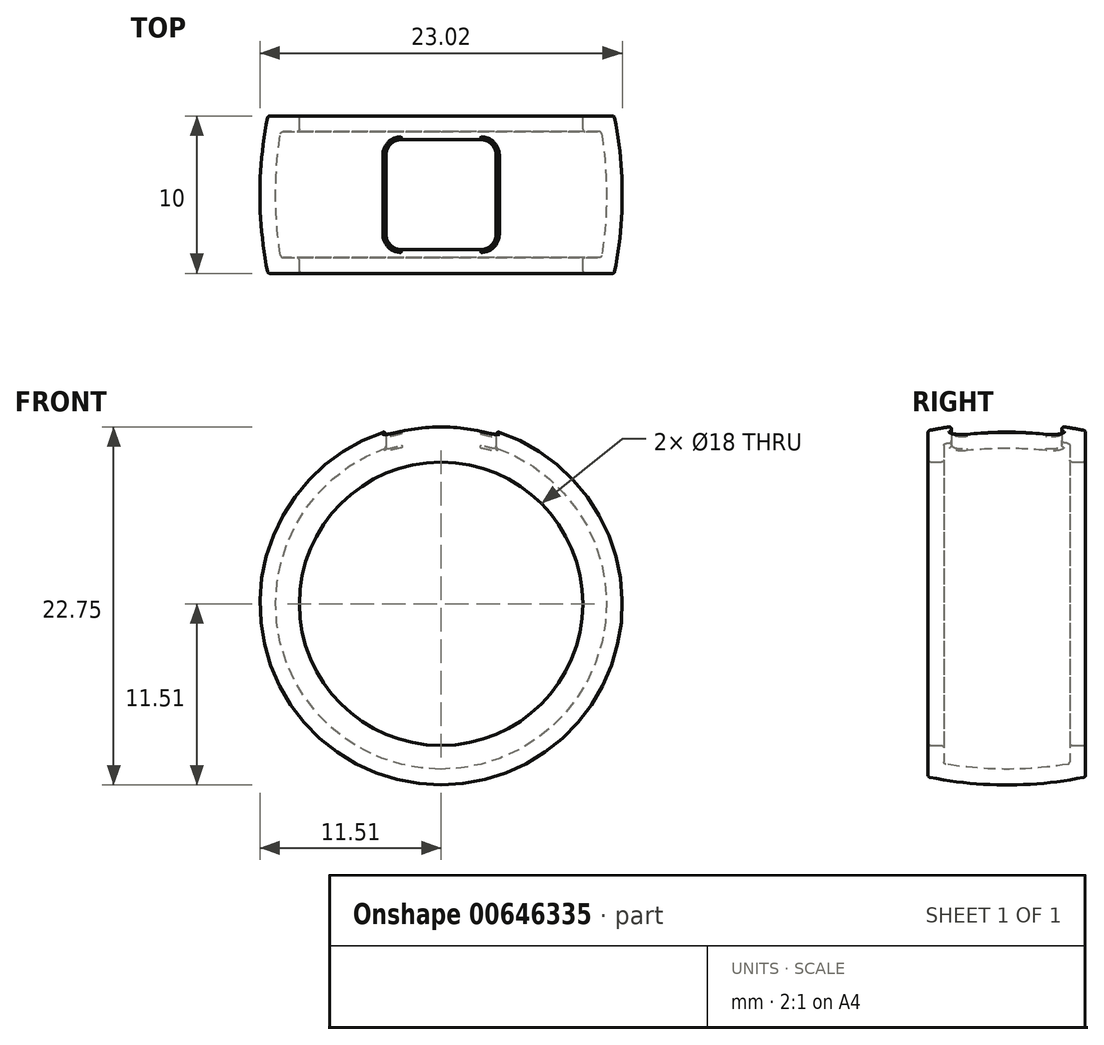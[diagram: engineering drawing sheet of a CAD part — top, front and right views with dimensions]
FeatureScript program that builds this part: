
annotation { "Feature Type Name" : "Feature", "Feature Type Description" : "" }
export const myFeature = defineFeature(function(context is Context, id is Id, definition is map)
    precondition{}
    {
        {
            var Q0;
            Q0=qCreatedBy(makeId("Top.planeOp"),FACE);
            var sketch = newSketch(context, id + "F0", { "sketchPlane" : qUnion([Q0])});
            skLineSegment(sketch, "E0", {"start": v(0, 0) * mm, "end": v(-9, 0) * mm, "construction": true});
            skLineSegment(sketch, "E1", {"start": v(-9, 5) * mm, "end": v(-9, -5) * mm});
            skLineSegment(sketch, "E2", {"start": v(-9, -5) * mm, "end": v(-11, -5) * mm});
            skLineSegment(sketch, "E3", {"start": v(-9, 5) * mm, "end": v(-11, 5) * mm});
            skArc(sketch, "E4", {"start": v(-11, 5) * mm, "mid": v(-11.5, 0) * mm, "end": v(-11, -5) * mm});
            skLineSegment(sketch, "E5", {"start": v(0, 0) * mm, "end": v(0, -20.5) * mm, "construction": true});
            skSolve(sketch);
        }
        {
            var Q0;
            Q0=makeQuery(id+"F0.imprint","IMPRINT",FACE,{"disambiguationData":[TD([[makeQuery(id+"F0.imprint","IMPRINT",EDGE,{"derivedFrom":sQuery(id+"F0.wireOp",EDGE,"E1")}),-1.0]])]});
            var Q1;
            Q1=sQuery(id+"F0.wireOp",EDGE,"E5");
            revolve(context, id + "F1", {"entities" : qUnion([Q0]), "axis" : qUnion([Q1]), "revolveType" : RevolveType.FULL});
        }
        {
            var Q0;
            Q0=makeQuery(id+"F1.opRevolve","SWEPT_FACE",FACE,{"disambiguationData":[OSD([sQuery(id+"F0.wireOp",EDGE,"E1")])]});
            shell(context, id + "F2", {"entities" : qUnion([Q0]), "thickness" : 1 * mm});
        }
        {
            var Q0;
            Q0=qCreatedBy(makeId("Top.planeOp"),FACE);
            var sketch = newSketch(context, id + "F3", { "sketchPlane" : qUnion([Q0])});
            skLineSegment(sketch, "E6.bottom", {"start": v(2.5, -3.5) * mm, "end": v(-2.5, -3.5) * mm});
            skLineSegment(sketch, "E6.top", {"start": v(2.5, 3.5) * mm, "end": v(-2.5, 3.5) * mm});
            skLineSegment(sketch, "E6.left", {"start": v(3.5, -2.5) * mm, "end": v(3.5, 2.5) * mm});
            skLineSegment(sketch, "E6.right", {"start": v(-3.5, -2.5) * mm, "end": v(-3.5, 2.5) * mm});
            skPoint(sketch, "E6.middle", {"position": v(0, 0) * mm});
            skPoint(sketch, "E7.visualSharp", {"position": v(-3.5, 3.5) * mm});
            skArc(sketch, "E7.filletArc", {"start": v(-2.5, 3.5) * mm, "mid": v(-3.2, 3.2) * mm, "end": v(-3.5, 2.5) * mm});
            skPoint(sketch, "E8.visualSharp", {"position": v(3.5, 3.5) * mm});
            skArc(sketch, "E8.filletArc", {"start": v(3.5, 2.5) * mm, "mid": v(3.2, 3.2) * mm, "end": v(2.5, 3.5) * mm});
            skPoint(sketch, "E9.visualSharp", {"position": v(-3.5, -3.5) * mm});
            skArc(sketch, "E9.filletArc", {"start": v(-3.5, -2.5) * mm, "mid": v(-3.2, -3.2) * mm, "end": v(-2.5, -3.5) * mm});
            skPoint(sketch, "E10.visualSharp", {"position": v(3.5, -3.5) * mm});
            skArc(sketch, "E10.filletArc", {"start": v(2.5, -3.5) * mm, "mid": v(3.2, -3.2) * mm, "end": v(3.5, -2.5) * mm});
            skSolve(sketch);
        }
        {
            var Q0;
            Q0 = qSketchRegion(id + "F3", true);
            extrude(context, id + "F4", {"entities" : qUnion([Q0]), "operationType" : NewBodyOperationType.REMOVE, "endBound" : BoundingType.THROUGH_ALL, "depth" : 25 * mm, "offsetDistance" : 25 * mm});
        }
        {
            var Q0;
            Q0=makeQuery(id+"F1.opRevolve","SWEPT_EDGE",EDGE,{"disambiguationData":[OSD([sQuery(id+"F0.wireOp",EDGE,"E1"),sQuery(id+"F0.wireOp",EDGE,"E3")])]});
            var Q1;
            Q1=makeQuery(id+"F1.opRevolve","SWEPT_EDGE",EDGE,{"disambiguationData":[OSD([sQuery(id+"F0.wireOp",EDGE,"E3"),sQuery(id+"F0.wireOp",EDGE,"E4")])]});
            var Q2;
            Q2=makeQuery(id+"FRUT5MbfFa7QnNZ_1.6.F4.boolean.opBoolean","INTERSECT",EDGE,{"derivedFrom":[makeQuery(id+"F2.opShell","OFFSET_FACE",FACE,{"disambiguationData":[OSD([sQuery(id+"F0.wireOp",EDGE,"E4")])]}),makeQuery(id+"FRUT5MbfFa7QnNZ_1.6.F4.opExtrude","SWEPT_FACE",FACE,{"disambiguationData":[OSD([sQuery(id+"F3.wireOp",EDGE,"E6.top")])]})]});
            var Q3;
            Q3=makeQuery(id+"FRUT5MbfFa7QnNZ_1.5.F4.boolean.opBoolean","INTERSECT",EDGE,{"derivedFrom":[makeQuery(id+"F2.opShell","OFFSET_FACE",FACE,{"disambiguationData":[OSD([sQuery(id+"F0.wireOp",EDGE,"E4")])]}),makeQuery(id+"FRUT5MbfFa7QnNZ_1.5.F4.opExtrude","SWEPT_FACE",FACE,{"disambiguationData":[OSD([sQuery(id+"F3.wireOp",EDGE,"E6.left")])]})]});
            var Q4;
            Q4=makeQuery(id+"FRUT5MbfFa7QnNZ_1.3.F4.boolean.opBoolean","INTERSECT",EDGE,{"derivedFrom":[makeQuery(id+"F2.opShell","OFFSET_FACE",FACE,{"disambiguationData":[OSD([sQuery(id+"F0.wireOp",EDGE,"E4")])]}),makeQuery(id+"FRUT5MbfFa7QnNZ_1.3.F4.opExtrude","SWEPT_FACE",FACE,{"disambiguationData":[OSD([sQuery(id+"F3.wireOp",EDGE,"E6.top")])]})]});
            var Q5;
            Q5=makeQuery(id+"FRUT5MbfFa7QnNZ_1.5.F4.boolean.opBoolean","INTERSECT",EDGE,{"derivedFrom":[makeQuery(id+"F2.opShell","OFFSET_FACE",FACE,{"disambiguationData":[OSD([sQuery(id+"F0.wireOp",EDGE,"E4")])]}),makeQuery(id+"FRUT5MbfFa7QnNZ_1.5.F4.opExtrude","SWEPT_FACE",FACE,{"disambiguationData":[OSD([sQuery(id+"F3.wireOp",EDGE,"E6.top")])]})]});
            var Q6;
            Q6=makeQuery(id+"FRUT5MbfFa7QnNZ_1.2.F4.boolean.opBoolean","INTERSECT",EDGE,{"derivedFrom":[makeQuery(id+"F2.opShell","OFFSET_FACE",FACE,{"disambiguationData":[OSD([sQuery(id+"F0.wireOp",EDGE,"E4")])]}),makeQuery(id+"FRUT5MbfFa7QnNZ_1.2.F4.opExtrude","SWEPT_FACE",FACE,{"disambiguationData":[OSD([sQuery(id+"F3.wireOp",EDGE,"E6.top")])]})]});
            var Q7;
            Q7=makeQuery(id+"FRUT5MbfFa7QnNZ_1.6.F4.boolean.opBoolean","INTERSECT",EDGE,{"derivedFrom":[makeQuery(id+"F2.opShell","OFFSET_FACE",FACE,{"disambiguationData":[OSD([sQuery(id+"F0.wireOp",EDGE,"E4")])]}),makeQuery(id+"FRUT5MbfFa7QnNZ_1.6.F4.opExtrude","SWEPT_FACE",FACE,{"disambiguationData":[OSD([sQuery(id+"F3.wireOp",EDGE,"E6.right")])]})]});
            var Q8;
            Q8=makeQuery(id+"FRUT5MbfFa7QnNZ_1.2.F4.boolean.opBoolean","INTERSECT",EDGE,{"derivedFrom":[makeQuery(id+"F2.opShell","OFFSET_FACE",FACE,{"disambiguationData":[OSD([sQuery(id+"F0.wireOp",EDGE,"E4")])]}),makeQuery(id+"FRUT5MbfFa7QnNZ_1.2.F4.opExtrude","SWEPT_FACE",FACE,{"disambiguationData":[OSD([sQuery(id+"F3.wireOp",EDGE,"E6.left")])]})]});
            var Q9;
            Q9=makeQuery(id+"F2.opShell","OFFSET_EDGE",EDGE,{"disambiguationData":[OSD([sQuery(id+"F0.wireOp",EDGE,"E3"),sQuery(id+"F0.wireOp",EDGE,"E4")])]});
            var Q10;
            Q10=makeQuery(id+"FRUT5MbfFa7QnNZ_1.4.F4.boolean.opBoolean","INTERSECT",EDGE,{"derivedFrom":[makeQuery(id+"F1.opRevolve","SWEPT_FACE",FACE,{"disambiguationData":[OSD([sQuery(id+"F0.wireOp",EDGE,"E4")])]}),makeQuery(id+"FRUT5MbfFa7QnNZ_1.4.F4.opExtrude","SWEPT_FACE",FACE,{"disambiguationData":[OSD([sQuery(id+"F3.wireOp",EDGE,"E6.bottom")])]})]});
            var Q11;
            Q11=makeQuery(id+"FRUT5MbfFa7QnNZ_1.4.F4.boolean.opBoolean","INTERSECT",EDGE,{"derivedFrom":[makeQuery(id+"F1.opRevolve","SWEPT_FACE",FACE,{"disambiguationData":[OSD([sQuery(id+"F0.wireOp",EDGE,"E4")])]}),makeQuery(id+"FRUT5MbfFa7QnNZ_1.4.F4.opExtrude","SWEPT_FACE",FACE,{"disambiguationData":[OSD([sQuery(id+"F3.wireOp",EDGE,"E6.left")])]})]});
            var Q12;
            Q12=makeQuery(id+"FRUT5MbfFa7QnNZ_1.5.F4.boolean.opBoolean","INTERSECT",EDGE,{"derivedFrom":[makeQuery(id+"F1.opRevolve","SWEPT_FACE",FACE,{"disambiguationData":[OSD([sQuery(id+"F0.wireOp",EDGE,"E4")])]}),makeQuery(id+"FRUT5MbfFa7QnNZ_1.5.F4.opExtrude","SWEPT_FACE",FACE,{"disambiguationData":[OSD([sQuery(id+"F3.wireOp",EDGE,"E6.right")])]})]});
            var Q13;
            Q13=makeQuery(id+"F1.opRevolve","SWEPT_EDGE",EDGE,{"disambiguationData":[OSD([sQuery(id+"F0.wireOp",EDGE,"E1"),sQuery(id+"F0.wireOp",EDGE,"E2")])]});
            var Q14;
            Q14=makeQuery(id+"F2.opShell","OFFSET_EDGE",EDGE,{"disambiguationData":[OSD([sQuery(id+"F0.wireOp",EDGE,"E1"),sQuery(id+"F0.wireOp",EDGE,"E3")])]});
            var Q15;
            Q15=makeQuery(id+"FRUT5MbfFa7QnNZ_1.4.F4.boolean.opBoolean","INTERSECT",EDGE,{"derivedFrom":[makeQuery(id+"F1.opRevolve","SWEPT_FACE",FACE,{"disambiguationData":[OSD([sQuery(id+"F0.wireOp",EDGE,"E4")])]}),makeQuery(id+"FRUT5MbfFa7QnNZ_1.4.F4.opExtrude","SWEPT_FACE",FACE,{"disambiguationData":[OSD([sQuery(id+"F3.wireOp",EDGE,"E6.top")])]})]});
            var Q16;
            Q16=makeQuery(id+"FRUT5MbfFa7QnNZ_1.5.F4.boolean.opBoolean","INTERSECT",EDGE,{"derivedFrom":[makeQuery(id+"F1.opRevolve","SWEPT_FACE",FACE,{"disambiguationData":[OSD([sQuery(id+"F0.wireOp",EDGE,"E4")])]}),makeQuery(id+"FRUT5MbfFa7QnNZ_1.5.F4.opExtrude","SWEPT_FACE",FACE,{"disambiguationData":[OSD([sQuery(id+"F3.wireOp",EDGE,"E6.bottom")])]})]});
            var Q17;
            Q17=makeQuery(id+"FRUT5MbfFa7QnNZ_1.5.F4.boolean.opBoolean","INTERSECT",EDGE,{"derivedFrom":[makeQuery(id+"F1.opRevolve","SWEPT_FACE",FACE,{"disambiguationData":[OSD([sQuery(id+"F0.wireOp",EDGE,"E4")])]}),makeQuery(id+"FRUT5MbfFa7QnNZ_1.5.F4.opExtrude","SWEPT_FACE",FACE,{"disambiguationData":[OSD([sQuery(id+"F3.wireOp",EDGE,"E6.left")])]})]});
            var Q18;
            Q18=makeQuery(id+"FRUT5MbfFa7QnNZ_1.6.F4.boolean.opBoolean","INTERSECT",EDGE,{"derivedFrom":[makeQuery(id+"F1.opRevolve","SWEPT_FACE",FACE,{"disambiguationData":[OSD([sQuery(id+"F0.wireOp",EDGE,"E4")])]}),makeQuery(id+"FRUT5MbfFa7QnNZ_1.6.F4.opExtrude","SWEPT_FACE",FACE,{"disambiguationData":[OSD([sQuery(id+"F3.wireOp",EDGE,"E6.right")])]})]});
            var Q19;
            Q19=makeQuery(id+"FRUT5MbfFa7QnNZ_1.6.F4.boolean.opBoolean","INTERSECT",EDGE,{"derivedFrom":[makeQuery(id+"F1.opRevolve","SWEPT_FACE",FACE,{"disambiguationData":[OSD([sQuery(id+"F0.wireOp",EDGE,"E4")])]}),makeQuery(id+"FRUT5MbfFa7QnNZ_1.6.F4.opExtrude","SWEPT_FACE",FACE,{"disambiguationData":[OSD([sQuery(id+"F3.wireOp",EDGE,"E6.bottom")])]})]});
            var Q20;
            Q20=makeQuery(id+"FRUT5MbfFa7QnNZ_1.6.F4.boolean.opBoolean","INTERSECT",EDGE,{"derivedFrom":[makeQuery(id+"F1.opRevolve","SWEPT_FACE",FACE,{"disambiguationData":[OSD([sQuery(id+"F0.wireOp",EDGE,"E4")])]}),makeQuery(id+"FRUT5MbfFa7QnNZ_1.6.F4.opExtrude","SWEPT_FACE",FACE,{"disambiguationData":[OSD([sQuery(id+"F3.wireOp",EDGE,"E6.left")])]})]});
            var Q21;
            Q21=makeQuery(id+"FRUT5MbfFa7QnNZ_1.6.F4.boolean.opBoolean","INTERSECT",EDGE,{"derivedFrom":[makeQuery(id+"F1.opRevolve","SWEPT_FACE",FACE,{"disambiguationData":[OSD([sQuery(id+"F0.wireOp",EDGE,"E4")])]}),makeQuery(id+"FRUT5MbfFa7QnNZ_1.6.F4.opExtrude","SWEPT_FACE",FACE,{"disambiguationData":[OSD([sQuery(id+"F3.wireOp",EDGE,"E6.top")])]})]});
            var Q22;
            Q22=makeQuery(id+"FRUT5MbfFa7QnNZ_1.1.F4.boolean.opBoolean","INTERSECT",EDGE,{"derivedFrom":[makeQuery(id+"F2.opShell","OFFSET_FACE",FACE,{"disambiguationData":[OSD([sQuery(id+"F0.wireOp",EDGE,"E4")])]}),makeQuery(id+"FRUT5MbfFa7QnNZ_1.1.F4.opExtrude","SWEPT_FACE",FACE,{"disambiguationData":[OSD([sQuery(id+"F3.wireOp",EDGE,"E6.right")])]})]});
            var Q23;
            Q23=makeQuery(id+"FRUT5MbfFa7QnNZ_1.5.F4.boolean.opBoolean","INTERSECT",EDGE,{"derivedFrom":[makeQuery(id+"F1.opRevolve","SWEPT_FACE",FACE,{"disambiguationData":[OSD([sQuery(id+"F0.wireOp",EDGE,"E4")])]}),makeQuery(id+"FRUT5MbfFa7QnNZ_1.5.F4.opExtrude","SWEPT_FACE",FACE,{"disambiguationData":[OSD([sQuery(id+"F3.wireOp",EDGE,"E6.top")])]})]});
            var Q24;
            Q24=makeQuery(id+"FRUT5MbfFa7QnNZ_1.1.F4.boolean.opBoolean","INTERSECT",EDGE,{"derivedFrom":[makeQuery(id+"F2.opShell","OFFSET_FACE",FACE,{"disambiguationData":[OSD([sQuery(id+"F0.wireOp",EDGE,"E4")])]}),makeQuery(id+"FRUT5MbfFa7QnNZ_1.1.F4.opExtrude","SWEPT_FACE",FACE,{"disambiguationData":[OSD([sQuery(id+"F3.wireOp",EDGE,"E6.top")])]})]});
            var Q25;
            Q25=makeQuery(id+"F2.opShell","OFFSET_EDGE",EDGE,{"disambiguationData":[OSD([sQuery(id+"F0.wireOp",EDGE,"E1"),sQuery(id+"F0.wireOp",EDGE,"E2")])]});
            var Q26;
            Q26=makeQuery(id+"F4.boolean.opBoolean","INTERSECT",EDGE,{"derivedFrom":[makeQuery(id+"F2.opShell","OFFSET_FACE",FACE,{"disambiguationData":[OSD([sQuery(id+"F0.wireOp",EDGE,"E4")])]}),makeQuery(id+"F4.opExtrude","SWEPT_FACE",FACE,{"disambiguationData":[OSD([sQuery(id+"F3.wireOp",EDGE,"E6.right")])]})]});
            var Q27;
            Q27=makeQuery(id+"F4.boolean.opBoolean","INTERSECT",EDGE,{"derivedFrom":[makeQuery(id+"F2.opShell","OFFSET_FACE",FACE,{"disambiguationData":[OSD([sQuery(id+"F0.wireOp",EDGE,"E4")])]}),makeQuery(id+"F4.opExtrude","SWEPT_FACE",FACE,{"disambiguationData":[OSD([sQuery(id+"F3.wireOp",EDGE,"E6.top")])]})]});
            var Q28;
            Q28=makeQuery(id+"FRUT5MbfFa7QnNZ_1.3.F4.boolean.opBoolean","INTERSECT",EDGE,{"derivedFrom":[makeQuery(id+"F2.opShell","OFFSET_FACE",FACE,{"disambiguationData":[OSD([sQuery(id+"F0.wireOp",EDGE,"E4")])]}),makeQuery(id+"FRUT5MbfFa7QnNZ_1.3.F4.opExtrude","SWEPT_FACE",FACE,{"disambiguationData":[OSD([sQuery(id+"F3.wireOp",EDGE,"E6.left")])]})]});
            var Q29;
            Q29=makeQuery(id+"FRUT5MbfFa7QnNZ_1.4.F4.boolean.opBoolean","COPY",EDGE,{"derivedFrom":makeQuery(id+"FRUT5MbfFa7QnNZ_1.4.F4.opExtrude","SWEPT_EDGE",EDGE,{"disambiguationData":[OSD([sQuery(id+"F3.wireOp",EDGE,"E6.top"),sQuery(id+"F3.wireOp",EDGE,"E8.filletArc")])]})});
            var Q30;
            Q30=makeQuery(id+"FRUT5MbfFa7QnNZ_1.2.F4.boolean.opBoolean","INTERSECT",EDGE,{"derivedFrom":[makeQuery(id+"F2.opShell","OFFSET_FACE",FACE,{"disambiguationData":[OSD([sQuery(id+"F0.wireOp",EDGE,"E4")])]}),makeQuery(id+"FRUT5MbfFa7QnNZ_1.2.F4.opExtrude","SWEPT_FACE",FACE,{"disambiguationData":[OSD([sQuery(id+"F3.wireOp",EDGE,"E6.right")])]})]});
            var Q31;
            Q31=makeQuery(id+"F1.opRevolve","SWEPT_EDGE",EDGE,{"disambiguationData":[OSD([sQuery(id+"F0.wireOp",EDGE,"E2"),sQuery(id+"F0.wireOp",EDGE,"E4")])]});
            var Q32;
            Q32=makeQuery(id+"F4.boolean.opBoolean","INTERSECT",EDGE,{"derivedFrom":[makeQuery(id+"F1.opRevolve","SWEPT_FACE",FACE,{"disambiguationData":[OSD([sQuery(id+"F0.wireOp",EDGE,"E4")])]}),makeQuery(id+"F4.opExtrude","SWEPT_FACE",FACE,{"disambiguationData":[OSD([sQuery(id+"F3.wireOp",EDGE,"E6.right")])]})]});
            var Q33;
            Q33=makeQuery(id+"F4.boolean.opBoolean","INTERSECT",EDGE,{"derivedFrom":[makeQuery(id+"F1.opRevolve","SWEPT_FACE",FACE,{"disambiguationData":[OSD([sQuery(id+"F0.wireOp",EDGE,"E4")])]}),makeQuery(id+"F4.opExtrude","SWEPT_FACE",FACE,{"disambiguationData":[OSD([sQuery(id+"F3.wireOp",EDGE,"E6.bottom")])]})]});
            var Q34;
            Q34=makeQuery(id+"F4.boolean.opBoolean","INTERSECT",EDGE,{"derivedFrom":[makeQuery(id+"F1.opRevolve","SWEPT_FACE",FACE,{"disambiguationData":[OSD([sQuery(id+"F0.wireOp",EDGE,"E4")])]}),makeQuery(id+"F4.opExtrude","SWEPT_FACE",FACE,{"disambiguationData":[OSD([sQuery(id+"F3.wireOp",EDGE,"E6.top")])]})]});
            var Q35;
            Q35=makeQuery(id+"F4.boolean.opBoolean","INTERSECT",EDGE,{"derivedFrom":[makeQuery(id+"F1.opRevolve","SWEPT_FACE",FACE,{"disambiguationData":[OSD([sQuery(id+"F0.wireOp",EDGE,"E4")])]}),makeQuery(id+"F4.opExtrude","SWEPT_FACE",FACE,{"disambiguationData":[OSD([sQuery(id+"F3.wireOp",EDGE,"E6.left")])]})]});
            var Q36;
            Q36=makeQuery(id+"FRUT5MbfFa7QnNZ_1.1.F4.boolean.opBoolean","INTERSECT",EDGE,{"derivedFrom":[makeQuery(id+"F1.opRevolve","SWEPT_FACE",FACE,{"disambiguationData":[OSD([sQuery(id+"F0.wireOp",EDGE,"E4")])]}),makeQuery(id+"FRUT5MbfFa7QnNZ_1.1.F4.opExtrude","SWEPT_FACE",FACE,{"disambiguationData":[OSD([sQuery(id+"F3.wireOp",EDGE,"E6.right")])]})]});
            var Q37;
            Q37=makeQuery(id+"FRUT5MbfFa7QnNZ_1.2.F4.boolean.opBoolean","INTERSECT",EDGE,{"derivedFrom":[makeQuery(id+"F1.opRevolve","SWEPT_FACE",FACE,{"disambiguationData":[OSD([sQuery(id+"F0.wireOp",EDGE,"E4")])]}),makeQuery(id+"FRUT5MbfFa7QnNZ_1.2.F4.opExtrude","SWEPT_FACE",FACE,{"disambiguationData":[OSD([sQuery(id+"F3.wireOp",EDGE,"E6.top")])]})]});
            var Q38;
            Q38=makeQuery(id+"FRUT5MbfFa7QnNZ_1.3.F4.boolean.opBoolean","INTERSECT",EDGE,{"derivedFrom":[makeQuery(id+"F1.opRevolve","SWEPT_FACE",FACE,{"disambiguationData":[OSD([sQuery(id+"F0.wireOp",EDGE,"E4")])]}),makeQuery(id+"FRUT5MbfFa7QnNZ_1.3.F4.opExtrude","SWEPT_FACE",FACE,{"disambiguationData":[OSD([sQuery(id+"F3.wireOp",EDGE,"E6.top")])]})]});
            var Q39;
            Q39=makeQuery(id+"FRUT5MbfFa7QnNZ_1.3.F4.boolean.opBoolean","INTERSECT",EDGE,{"derivedFrom":[makeQuery(id+"F1.opRevolve","SWEPT_FACE",FACE,{"disambiguationData":[OSD([sQuery(id+"F0.wireOp",EDGE,"E4")])]}),makeQuery(id+"FRUT5MbfFa7QnNZ_1.3.F4.opExtrude","SWEPT_FACE",FACE,{"disambiguationData":[OSD([sQuery(id+"F3.wireOp",EDGE,"E6.left")])]})]});
            var Q40;
            Q40=makeQuery(id+"FRUT5MbfFa7QnNZ_1.4.F4.boolean.opBoolean","INTERSECT",EDGE,{"derivedFrom":[makeQuery(id+"F1.opRevolve","SWEPT_FACE",FACE,{"disambiguationData":[OSD([sQuery(id+"F0.wireOp",EDGE,"E4")])]}),makeQuery(id+"FRUT5MbfFa7QnNZ_1.4.F4.opExtrude","SWEPT_FACE",FACE,{"disambiguationData":[OSD([sQuery(id+"F3.wireOp",EDGE,"E6.right")])]})]});
            var Q41;
            Q41=makeQuery(id+"FRUT5MbfFa7QnNZ_1.2.F4.boolean.opBoolean","INTERSECT",EDGE,{"derivedFrom":[makeQuery(id+"F1.opRevolve","SWEPT_FACE",FACE,{"disambiguationData":[OSD([sQuery(id+"F0.wireOp",EDGE,"E4")])]}),makeQuery(id+"FRUT5MbfFa7QnNZ_1.2.F4.opExtrude","SWEPT_FACE",FACE,{"disambiguationData":[OSD([sQuery(id+"F3.wireOp",EDGE,"E6.right")])]})]});
            var Q42;
            Q42=makeQuery(id+"FRUT5MbfFa7QnNZ_1.5.F4.boolean.opBoolean","COPY",EDGE,{"derivedFrom":makeQuery(id+"FRUT5MbfFa7QnNZ_1.5.F4.opExtrude","SWEPT_EDGE",EDGE,{"disambiguationData":[OSD([sQuery(id+"F3.wireOp",EDGE,"E6.left"),sQuery(id+"F3.wireOp",EDGE,"E10.filletArc")])]})});
            var Q43;
            Q43=makeQuery(id+"FRUT5MbfFa7QnNZ_1.3.F4.boolean.opBoolean","COPY",EDGE,{"derivedFrom":makeQuery(id+"FRUT5MbfFa7QnNZ_1.3.F4.opExtrude","SWEPT_EDGE",EDGE,{"disambiguationData":[OSD([sQuery(id+"F3.wireOp",EDGE,"E6.left"),sQuery(id+"F3.wireOp",EDGE,"E8.filletArc")])]})});
            var Q44;
            Q44=makeQuery(id+"FRUT5MbfFa7QnNZ_1.5.F4.boolean.opBoolean","INTERSECT",EDGE,{"derivedFrom":[makeQuery(id+"F2.opShell","OFFSET_FACE",FACE,{"disambiguationData":[OSD([sQuery(id+"F0.wireOp",EDGE,"E4")])]}),makeQuery(id+"FRUT5MbfFa7QnNZ_1.5.F4.opExtrude","SWEPT_FACE",FACE,{"disambiguationData":[OSD([sQuery(id+"F3.wireOp",EDGE,"E10.filletArc")])]})]});
            var Q45;
            Q45=makeQuery(id+"F4.boolean.opBoolean","COPY",EDGE,{"derivedFrom":makeQuery(id+"F4.opExtrude","SWEPT_EDGE",EDGE,{"disambiguationData":[OSD([sQuery(id+"F3.wireOp",EDGE,"E6.left"),sQuery(id+"F3.wireOp",EDGE,"E10.filletArc")])]})});
            var Q46;
            Q46=makeQuery(id+"FRUT5MbfFa7QnNZ_1.6.F4.boolean.opBoolean","COPY",EDGE,{"derivedFrom":makeQuery(id+"FRUT5MbfFa7QnNZ_1.6.F4.opExtrude","SWEPT_EDGE",EDGE,{"disambiguationData":[OSD([sQuery(id+"F3.wireOp",EDGE,"E6.left"),sQuery(id+"F3.wireOp",EDGE,"E8.filletArc")])]})});
            var Q47;
            Q47=makeQuery(id+"FRUT5MbfFa7QnNZ_1.6.F4.boolean.opBoolean","COPY",EDGE,{"derivedFrom":makeQuery(id+"FRUT5MbfFa7QnNZ_1.6.F4.opExtrude","SWEPT_EDGE",EDGE,{"disambiguationData":[OSD([sQuery(id+"F3.wireOp",EDGE,"E6.right"),sQuery(id+"F3.wireOp",EDGE,"E9.filletArc")])]})});
            var Q48;
            Q48=makeQuery(id+"F4.boolean.opBoolean","COPY",EDGE,{"derivedFrom":makeQuery(id+"F4.opExtrude","SWEPT_EDGE",EDGE,{"disambiguationData":[OSD([sQuery(id+"F3.wireOp",EDGE,"E6.top"),sQuery(id+"F3.wireOp",EDGE,"E7.filletArc")])]})});
            var Q49;
            Q49=makeQuery(id+"FRUT5MbfFa7QnNZ_1.3.F4.boolean.opBoolean","COPY",EDGE,{"derivedFrom":makeQuery(id+"FRUT5MbfFa7QnNZ_1.3.F4.opExtrude","SWEPT_EDGE",EDGE,{"disambiguationData":[OSD([sQuery(id+"F3.wireOp",EDGE,"E6.left"),sQuery(id+"F3.wireOp",EDGE,"E10.filletArc")])]})});
            var Q50;
            Q50=makeQuery(id+"FRUT5MbfFa7QnNZ_1.5.F4.boolean.opBoolean","COPY",EDGE,{"derivedFrom":makeQuery(id+"FRUT5MbfFa7QnNZ_1.5.F4.opExtrude","SWEPT_EDGE",EDGE,{"disambiguationData":[OSD([sQuery(id+"F3.wireOp",EDGE,"E6.right"),sQuery(id+"F3.wireOp",EDGE,"E7.filletArc")])]})});
            var Q51;
            Q51=makeQuery(id+"FRUT5MbfFa7QnNZ_1.4.F4.boolean.opBoolean","COPY",EDGE,{"derivedFrom":makeQuery(id+"FRUT5MbfFa7QnNZ_1.4.F4.opExtrude","SWEPT_EDGE",EDGE,{"disambiguationData":[OSD([sQuery(id+"F3.wireOp",EDGE,"E6.left"),sQuery(id+"F3.wireOp",EDGE,"E8.filletArc")])]})});
            var Q52;
            Q52=makeQuery(id+"FRUT5MbfFa7QnNZ_1.1.F4.boolean.opBoolean","INTERSECT",EDGE,{"derivedFrom":[makeQuery(id+"F2.opShell","OFFSET_FACE",FACE,{"disambiguationData":[OSD([sQuery(id+"F0.wireOp",EDGE,"E4")])]}),makeQuery(id+"FRUT5MbfFa7QnNZ_1.1.F4.opExtrude","SWEPT_FACE",FACE,{"disambiguationData":[OSD([sQuery(id+"F3.wireOp",EDGE,"E6.bottom")])]})]});
            var Q53;
            Q53=makeQuery(id+"FRUT5MbfFa7QnNZ_1.4.F4.boolean.opBoolean","COPY",EDGE,{"derivedFrom":makeQuery(id+"FRUT5MbfFa7QnNZ_1.4.F4.opExtrude","SWEPT_EDGE",EDGE,{"disambiguationData":[OSD([sQuery(id+"F3.wireOp",EDGE,"E6.right"),sQuery(id+"F3.wireOp",EDGE,"E7.filletArc")])]})});
            var Q54;
            Q54=makeQuery(id+"FRUT5MbfFa7QnNZ_1.2.F4.boolean.opBoolean","COPY",EDGE,{"derivedFrom":makeQuery(id+"FRUT5MbfFa7QnNZ_1.2.F4.opExtrude","SWEPT_EDGE",EDGE,{"disambiguationData":[OSD([sQuery(id+"F3.wireOp",EDGE,"E6.top"),sQuery(id+"F3.wireOp",EDGE,"E7.filletArc")])]})});
            var Q55;
            Q55=makeQuery(id+"FRUT5MbfFa7QnNZ_1.5.F4.boolean.opBoolean","INTERSECT",EDGE,{"derivedFrom":[makeQuery(id+"F2.opShell","OFFSET_FACE",FACE,{"disambiguationData":[OSD([sQuery(id+"F0.wireOp",EDGE,"E4")])]}),makeQuery(id+"FRUT5MbfFa7QnNZ_1.5.F4.opExtrude","SWEPT_FACE",FACE,{"disambiguationData":[OSD([sQuery(id+"F3.wireOp",EDGE,"E9.filletArc")])]})]});
            var Q56;
            Q56=makeQuery(id+"FRUT5MbfFa7QnNZ_1.2.F4.boolean.opBoolean","COPY",EDGE,{"derivedFrom":makeQuery(id+"FRUT5MbfFa7QnNZ_1.2.F4.opExtrude","SWEPT_EDGE",EDGE,{"disambiguationData":[OSD([sQuery(id+"F3.wireOp",EDGE,"E6.right"),sQuery(id+"F3.wireOp",EDGE,"E7.filletArc")])]})});
            var Q57;
            Q57=makeQuery(id+"FRUT5MbfFa7QnNZ_1.6.F4.boolean.opBoolean","INTERSECT",EDGE,{"derivedFrom":[makeQuery(id+"F2.opShell","OFFSET_FACE",FACE,{"disambiguationData":[OSD([sQuery(id+"F0.wireOp",EDGE,"E4")])]}),makeQuery(id+"FRUT5MbfFa7QnNZ_1.6.F4.opExtrude","SWEPT_FACE",FACE,{"disambiguationData":[OSD([sQuery(id+"F3.wireOp",EDGE,"E8.filletArc")])]})]});
            var Q58;
            Q58=makeQuery(id+"FRUT5MbfFa7QnNZ_1.2.F4.boolean.opBoolean","INTERSECT",EDGE,{"derivedFrom":[makeQuery(id+"F2.opShell","OFFSET_FACE",FACE,{"disambiguationData":[OSD([sQuery(id+"F0.wireOp",EDGE,"E4")])]}),makeQuery(id+"FRUT5MbfFa7QnNZ_1.2.F4.opExtrude","SWEPT_FACE",FACE,{"disambiguationData":[OSD([sQuery(id+"F3.wireOp",EDGE,"E10.filletArc")])]})]});
            var Q59;
            Q59=makeQuery(id+"FRUT5MbfFa7QnNZ_1.6.F4.boolean.opBoolean","INTERSECT",EDGE,{"derivedFrom":[makeQuery(id+"F2.opShell","OFFSET_FACE",FACE,{"disambiguationData":[OSD([sQuery(id+"F0.wireOp",EDGE,"E4")])]}),makeQuery(id+"FRUT5MbfFa7QnNZ_1.6.F4.opExtrude","SWEPT_FACE",FACE,{"disambiguationData":[OSD([sQuery(id+"F3.wireOp",EDGE,"E10.filletArc")])]})]});
            var Q60;
            Q60=makeQuery(id+"FRUT5MbfFa7QnNZ_1.3.F4.boolean.opBoolean","INTERSECT",EDGE,{"derivedFrom":[makeQuery(id+"F2.opShell","OFFSET_FACE",FACE,{"disambiguationData":[OSD([sQuery(id+"F0.wireOp",EDGE,"E4")])]}),makeQuery(id+"FRUT5MbfFa7QnNZ_1.3.F4.opExtrude","SWEPT_FACE",FACE,{"disambiguationData":[OSD([sQuery(id+"F3.wireOp",EDGE,"E8.filletArc")])]})]});
            var Q61;
            Q61=makeQuery(id+"FRUT5MbfFa7QnNZ_1.4.F4.boolean.opBoolean","INTERSECT",EDGE,{"derivedFrom":[makeQuery(id+"F2.opShell","OFFSET_FACE",FACE,{"disambiguationData":[OSD([sQuery(id+"F0.wireOp",EDGE,"E4")])]}),makeQuery(id+"FRUT5MbfFa7QnNZ_1.4.F4.opExtrude","SWEPT_FACE",FACE,{"disambiguationData":[OSD([sQuery(id+"F3.wireOp",EDGE,"E6.right")])]})]});
            var Q62;
            Q62=makeQuery(id+"FRUT5MbfFa7QnNZ_1.4.F4.boolean.opBoolean","COPY",EDGE,{"derivedFrom":makeQuery(id+"FRUT5MbfFa7QnNZ_1.4.F4.opExtrude","SWEPT_EDGE",EDGE,{"disambiguationData":[OSD([sQuery(id+"F3.wireOp",EDGE,"E6.bottom"),sQuery(id+"F3.wireOp",EDGE,"E9.filletArc")])]})});
            var Q63;
            Q63=makeQuery(id+"FRUT5MbfFa7QnNZ_1.3.F4.boolean.opBoolean","INTERSECT",EDGE,{"derivedFrom":[makeQuery(id+"F2.opShell","OFFSET_FACE",FACE,{"disambiguationData":[OSD([sQuery(id+"F0.wireOp",EDGE,"E4")])]}),makeQuery(id+"FRUT5MbfFa7QnNZ_1.3.F4.opExtrude","SWEPT_FACE",FACE,{"disambiguationData":[OSD([sQuery(id+"F3.wireOp",EDGE,"E6.bottom")])]})]});
            var Q64;
            Q64=makeQuery(id+"FRUT5MbfFa7QnNZ_1.5.F4.boolean.opBoolean","INTERSECT",EDGE,{"derivedFrom":[makeQuery(id+"F2.opShell","OFFSET_FACE",FACE,{"disambiguationData":[OSD([sQuery(id+"F0.wireOp",EDGE,"E4")])]}),makeQuery(id+"FRUT5MbfFa7QnNZ_1.5.F4.opExtrude","SWEPT_FACE",FACE,{"disambiguationData":[OSD([sQuery(id+"F3.wireOp",EDGE,"E6.bottom")])]})]});
            var Q65;
            Q65=makeQuery(id+"FRUT5MbfFa7QnNZ_1.4.F4.boolean.opBoolean","INTERSECT",EDGE,{"derivedFrom":[makeQuery(id+"F2.opShell","OFFSET_FACE",FACE,{"disambiguationData":[OSD([sQuery(id+"F0.wireOp",EDGE,"E4")])]}),makeQuery(id+"FRUT5MbfFa7QnNZ_1.4.F4.opExtrude","SWEPT_FACE",FACE,{"disambiguationData":[OSD([sQuery(id+"F3.wireOp",EDGE,"E6.left")])]})]});
            var Q66;
            Q66=makeQuery(id+"FRUT5MbfFa7QnNZ_1.6.F4.boolean.opBoolean","COPY",EDGE,{"derivedFrom":makeQuery(id+"FRUT5MbfFa7QnNZ_1.6.F4.opExtrude","SWEPT_EDGE",EDGE,{"disambiguationData":[OSD([sQuery(id+"F3.wireOp",EDGE,"E6.top"),sQuery(id+"F3.wireOp",EDGE,"E7.filletArc")])]})});
            var Q67;
            Q67=makeQuery(id+"FRUT5MbfFa7QnNZ_1.1.F4.boolean.opBoolean","INTERSECT",EDGE,{"derivedFrom":[makeQuery(id+"F2.opShell","OFFSET_FACE",FACE,{"disambiguationData":[OSD([sQuery(id+"F0.wireOp",EDGE,"E4")])]}),makeQuery(id+"FRUT5MbfFa7QnNZ_1.1.F4.opExtrude","SWEPT_FACE",FACE,{"disambiguationData":[OSD([sQuery(id+"F3.wireOp",EDGE,"E9.filletArc")])]})]});
            var Q68;
            Q68=makeQuery(id+"FRUT5MbfFa7QnNZ_1.1.F4.boolean.opBoolean","COPY",EDGE,{"derivedFrom":makeQuery(id+"FRUT5MbfFa7QnNZ_1.1.F4.opExtrude","SWEPT_EDGE",EDGE,{"disambiguationData":[OSD([sQuery(id+"F3.wireOp",EDGE,"E6.right"),sQuery(id+"F3.wireOp",EDGE,"E7.filletArc")])]})});
            var Q69;
            Q69=makeQuery(id+"FRUT5MbfFa7QnNZ_1.1.F4.boolean.opBoolean","COPY",EDGE,{"derivedFrom":makeQuery(id+"FRUT5MbfFa7QnNZ_1.1.F4.opExtrude","SWEPT_EDGE",EDGE,{"disambiguationData":[OSD([sQuery(id+"F3.wireOp",EDGE,"E6.top"),sQuery(id+"F3.wireOp",EDGE,"E7.filletArc")])]})});
            var Q70;
            Q70=makeQuery(id+"F2.opShell","OFFSET_EDGE",EDGE,{"disambiguationData":[OSD([sQuery(id+"F0.wireOp",EDGE,"E2"),sQuery(id+"F0.wireOp",EDGE,"E4")])]});
            var Q71;
            Q71=makeQuery(id+"FRUT5MbfFa7QnNZ_1.6.F4.boolean.opBoolean","INTERSECT",EDGE,{"derivedFrom":[makeQuery(id+"F2.opShell","OFFSET_FACE",FACE,{"disambiguationData":[OSD([sQuery(id+"F0.wireOp",EDGE,"E4")])]}),makeQuery(id+"FRUT5MbfFa7QnNZ_1.6.F4.opExtrude","SWEPT_FACE",FACE,{"disambiguationData":[OSD([sQuery(id+"F3.wireOp",EDGE,"E7.filletArc")])]})]});
            var Q72;
            Q72=makeQuery(id+"FRUT5MbfFa7QnNZ_1.6.F4.boolean.opBoolean","INTERSECT",EDGE,{"derivedFrom":[makeQuery(id+"F2.opShell","OFFSET_FACE",FACE,{"disambiguationData":[OSD([sQuery(id+"F0.wireOp",EDGE,"E4")])]}),makeQuery(id+"FRUT5MbfFa7QnNZ_1.6.F4.opExtrude","SWEPT_FACE",FACE,{"disambiguationData":[OSD([sQuery(id+"F3.wireOp",EDGE,"E9.filletArc")])]})]});
            var Q73;
            Q73=makeQuery(id+"FRUT5MbfFa7QnNZ_1.6.F4.boolean.opBoolean","COPY",EDGE,{"derivedFrom":makeQuery(id+"FRUT5MbfFa7QnNZ_1.6.F4.opExtrude","SWEPT_EDGE",EDGE,{"disambiguationData":[OSD([sQuery(id+"F3.wireOp",EDGE,"E6.top"),sQuery(id+"F3.wireOp",EDGE,"E8.filletArc")])]})});
            var Q74;
            Q74=makeQuery(id+"FRUT5MbfFa7QnNZ_1.6.F4.boolean.opBoolean","COPY",EDGE,{"derivedFrom":makeQuery(id+"FRUT5MbfFa7QnNZ_1.6.F4.opExtrude","SWEPT_EDGE",EDGE,{"disambiguationData":[OSD([sQuery(id+"F3.wireOp",EDGE,"E6.right"),sQuery(id+"F3.wireOp",EDGE,"E7.filletArc")])]})});
            var Q75;
            Q75=makeQuery(id+"FRUT5MbfFa7QnNZ_1.5.F4.boolean.opBoolean","COPY",EDGE,{"derivedFrom":makeQuery(id+"FRUT5MbfFa7QnNZ_1.5.F4.opExtrude","SWEPT_EDGE",EDGE,{"disambiguationData":[OSD([sQuery(id+"F3.wireOp",EDGE,"E6.top"),sQuery(id+"F3.wireOp",EDGE,"E7.filletArc")])]})});
            var Q76;
            Q76=makeQuery(id+"F4.boolean.opBoolean","INTERSECT",EDGE,{"derivedFrom":[makeQuery(id+"F1.opRevolve","SWEPT_FACE",FACE,{"disambiguationData":[OSD([sQuery(id+"F0.wireOp",EDGE,"E4")])]}),makeQuery(id+"F4.opExtrude","SWEPT_FACE",FACE,{"disambiguationData":[OSD([sQuery(id+"F3.wireOp",EDGE,"E7.filletArc")])]})]});
            var Q77;
            Q77=makeQuery(id+"F4.boolean.opBoolean","INTERSECT",EDGE,{"derivedFrom":[makeQuery(id+"F1.opRevolve","SWEPT_FACE",FACE,{"disambiguationData":[OSD([sQuery(id+"F0.wireOp",EDGE,"E4")])]}),makeQuery(id+"F4.opExtrude","SWEPT_FACE",FACE,{"disambiguationData":[OSD([sQuery(id+"F3.wireOp",EDGE,"E10.filletArc")])]})]});
            var Q78;
            Q78=makeQuery(id+"FRUT5MbfFa7QnNZ_1.1.F4.boolean.opBoolean","INTERSECT",EDGE,{"derivedFrom":[makeQuery(id+"F1.opRevolve","SWEPT_FACE",FACE,{"disambiguationData":[OSD([sQuery(id+"F0.wireOp",EDGE,"E4")])]}),makeQuery(id+"FRUT5MbfFa7QnNZ_1.1.F4.opExtrude","SWEPT_FACE",FACE,{"disambiguationData":[OSD([sQuery(id+"F3.wireOp",EDGE,"E7.filletArc")])]})]});
            var Q79;
            Q79=makeQuery(id+"FRUT5MbfFa7QnNZ_1.2.F4.boolean.opBoolean","INTERSECT",EDGE,{"derivedFrom":[makeQuery(id+"F1.opRevolve","SWEPT_FACE",FACE,{"disambiguationData":[OSD([sQuery(id+"F0.wireOp",EDGE,"E4")])]}),makeQuery(id+"FRUT5MbfFa7QnNZ_1.2.F4.opExtrude","SWEPT_FACE",FACE,{"disambiguationData":[OSD([sQuery(id+"F3.wireOp",EDGE,"E7.filletArc")])]})]});
            var Q80;
            Q80=makeQuery(id+"FRUT5MbfFa7QnNZ_1.2.F4.boolean.opBoolean","INTERSECT",EDGE,{"derivedFrom":[makeQuery(id+"F1.opRevolve","SWEPT_FACE",FACE,{"disambiguationData":[OSD([sQuery(id+"F0.wireOp",EDGE,"E4")])]}),makeQuery(id+"FRUT5MbfFa7QnNZ_1.2.F4.opExtrude","SWEPT_FACE",FACE,{"disambiguationData":[OSD([sQuery(id+"F3.wireOp",EDGE,"E10.filletArc")])]})]});
            var Q81;
            Q81=makeQuery(id+"FRUT5MbfFa7QnNZ_1.4.F4.boolean.opBoolean","INTERSECT",EDGE,{"derivedFrom":[makeQuery(id+"F1.opRevolve","SWEPT_FACE",FACE,{"disambiguationData":[OSD([sQuery(id+"F0.wireOp",EDGE,"E4")])]}),makeQuery(id+"FRUT5MbfFa7QnNZ_1.4.F4.opExtrude","SWEPT_FACE",FACE,{"disambiguationData":[OSD([sQuery(id+"F3.wireOp",EDGE,"E7.filletArc")])]})]});
            var Q82;
            Q82=makeQuery(id+"FRUT5MbfFa7QnNZ_1.4.F4.boolean.opBoolean","INTERSECT",EDGE,{"derivedFrom":[makeQuery(id+"F1.opRevolve","SWEPT_FACE",FACE,{"disambiguationData":[OSD([sQuery(id+"F0.wireOp",EDGE,"E4")])]}),makeQuery(id+"FRUT5MbfFa7QnNZ_1.4.F4.opExtrude","SWEPT_FACE",FACE,{"disambiguationData":[OSD([sQuery(id+"F3.wireOp",EDGE,"E9.filletArc")])]})]});
            var Q83;
            Q83=makeQuery(id+"FRUT5MbfFa7QnNZ_1.6.F4.boolean.opBoolean","INTERSECT",EDGE,{"derivedFrom":[makeQuery(id+"F1.opRevolve","SWEPT_FACE",FACE,{"disambiguationData":[OSD([sQuery(id+"F0.wireOp",EDGE,"E4")])]}),makeQuery(id+"FRUT5MbfFa7QnNZ_1.6.F4.opExtrude","SWEPT_FACE",FACE,{"disambiguationData":[OSD([sQuery(id+"F3.wireOp",EDGE,"E8.filletArc")])]})]});
            var Q84;
            Q84=makeQuery(id+"FRUT5MbfFa7QnNZ_1.6.F4.boolean.opBoolean","INTERSECT",EDGE,{"derivedFrom":[makeQuery(id+"F1.opRevolve","SWEPT_FACE",FACE,{"disambiguationData":[OSD([sQuery(id+"F0.wireOp",EDGE,"E4")])]}),makeQuery(id+"FRUT5MbfFa7QnNZ_1.6.F4.opExtrude","SWEPT_FACE",FACE,{"disambiguationData":[OSD([sQuery(id+"F3.wireOp",EDGE,"E9.filletArc")])]})]});
            var Q85;
            Q85=makeQuery(id+"FRUT5MbfFa7QnNZ_1.5.F4.boolean.opBoolean","INTERSECT",EDGE,{"derivedFrom":[makeQuery(id+"F1.opRevolve","SWEPT_FACE",FACE,{"disambiguationData":[OSD([sQuery(id+"F0.wireOp",EDGE,"E4")])]}),makeQuery(id+"FRUT5MbfFa7QnNZ_1.5.F4.opExtrude","SWEPT_FACE",FACE,{"disambiguationData":[OSD([sQuery(id+"F3.wireOp",EDGE,"E9.filletArc")])]})]});
            var Q86;
            Q86=makeQuery(id+"FRUT5MbfFa7QnNZ_1.5.F4.boolean.opBoolean","INTERSECT",EDGE,{"derivedFrom":[makeQuery(id+"F1.opRevolve","SWEPT_FACE",FACE,{"disambiguationData":[OSD([sQuery(id+"F0.wireOp",EDGE,"E4")])]}),makeQuery(id+"FRUT5MbfFa7QnNZ_1.5.F4.opExtrude","SWEPT_FACE",FACE,{"disambiguationData":[OSD([sQuery(id+"F3.wireOp",EDGE,"E7.filletArc")])]})]});
            var Q87;
            Q87=makeQuery(id+"FRUT5MbfFa7QnNZ_1.6.F4.boolean.opBoolean","INTERSECT",EDGE,{"derivedFrom":[makeQuery(id+"F1.opRevolve","SWEPT_FACE",FACE,{"disambiguationData":[OSD([sQuery(id+"F0.wireOp",EDGE,"E4")])]}),makeQuery(id+"FRUT5MbfFa7QnNZ_1.6.F4.opExtrude","SWEPT_FACE",FACE,{"disambiguationData":[OSD([sQuery(id+"F3.wireOp",EDGE,"E10.filletArc")])]})]});
            var Q88;
            Q88=makeQuery(id+"FRUT5MbfFa7QnNZ_1.4.F4.boolean.opBoolean","INTERSECT",EDGE,{"derivedFrom":[makeQuery(id+"F2.opShell","OFFSET_FACE",FACE,{"disambiguationData":[OSD([sQuery(id+"F0.wireOp",EDGE,"E4")])]}),makeQuery(id+"FRUT5MbfFa7QnNZ_1.4.F4.opExtrude","SWEPT_FACE",FACE,{"disambiguationData":[OSD([sQuery(id+"F3.wireOp",EDGE,"E6.bottom")])]})]});
            var Q89;
            Q89=makeQuery(id+"FRUT5MbfFa7QnNZ_1.3.F4.boolean.opBoolean","INTERSECT",EDGE,{"derivedFrom":[makeQuery(id+"F2.opShell","OFFSET_FACE",FACE,{"disambiguationData":[OSD([sQuery(id+"F0.wireOp",EDGE,"E4")])]}),makeQuery(id+"FRUT5MbfFa7QnNZ_1.3.F4.opExtrude","SWEPT_FACE",FACE,{"disambiguationData":[OSD([sQuery(id+"F3.wireOp",EDGE,"E10.filletArc")])]})]});
            var Q90;
            Q90=makeQuery(id+"FRUT5MbfFa7QnNZ_1.4.F4.boolean.opBoolean","INTERSECT",EDGE,{"derivedFrom":[makeQuery(id+"F2.opShell","OFFSET_FACE",FACE,{"disambiguationData":[OSD([sQuery(id+"F0.wireOp",EDGE,"E4")])]}),makeQuery(id+"FRUT5MbfFa7QnNZ_1.4.F4.opExtrude","SWEPT_FACE",FACE,{"disambiguationData":[OSD([sQuery(id+"F3.wireOp",EDGE,"E8.filletArc")])]})]});
            var Q91;
            Q91=makeQuery(id+"F4.boolean.opBoolean","INTERSECT",EDGE,{"derivedFrom":[makeQuery(id+"F2.opShell","OFFSET_FACE",FACE,{"disambiguationData":[OSD([sQuery(id+"F0.wireOp",EDGE,"E4")])]}),makeQuery(id+"F4.opExtrude","SWEPT_FACE",FACE,{"disambiguationData":[OSD([sQuery(id+"F3.wireOp",EDGE,"E6.left")])]})]});
            var Q92;
            Q92=makeQuery(id+"FRUT5MbfFa7QnNZ_1.2.F4.boolean.opBoolean","INTERSECT",EDGE,{"derivedFrom":[makeQuery(id+"F2.opShell","OFFSET_FACE",FACE,{"disambiguationData":[OSD([sQuery(id+"F0.wireOp",EDGE,"E4")])]}),makeQuery(id+"FRUT5MbfFa7QnNZ_1.2.F4.opExtrude","SWEPT_FACE",FACE,{"disambiguationData":[OSD([sQuery(id+"F3.wireOp",EDGE,"E6.bottom")])]})]});
            var Q93;
            Q93=makeQuery(id+"FRUT5MbfFa7QnNZ_1.4.F4.boolean.opBoolean","INTERSECT",EDGE,{"derivedFrom":[makeQuery(id+"F2.opShell","OFFSET_FACE",FACE,{"disambiguationData":[OSD([sQuery(id+"F0.wireOp",EDGE,"E4")])]}),makeQuery(id+"FRUT5MbfFa7QnNZ_1.4.F4.opExtrude","SWEPT_FACE",FACE,{"disambiguationData":[OSD([sQuery(id+"F3.wireOp",EDGE,"E6.top")])]})]});
            var Q94;
            Q94=makeQuery(id+"FRUT5MbfFa7QnNZ_1.4.F4.boolean.opBoolean","INTERSECT",EDGE,{"derivedFrom":[makeQuery(id+"F2.opShell","OFFSET_FACE",FACE,{"disambiguationData":[OSD([sQuery(id+"F0.wireOp",EDGE,"E4")])]}),makeQuery(id+"FRUT5MbfFa7QnNZ_1.4.F4.opExtrude","SWEPT_FACE",FACE,{"disambiguationData":[OSD([sQuery(id+"F3.wireOp",EDGE,"E7.filletArc")])]})]});
            var Q95;
            Q95=makeQuery(id+"FRUT5MbfFa7QnNZ_1.5.F4.boolean.opBoolean","COPY",EDGE,{"derivedFrom":makeQuery(id+"FRUT5MbfFa7QnNZ_1.5.F4.opExtrude","SWEPT_EDGE",EDGE,{"disambiguationData":[OSD([sQuery(id+"F3.wireOp",EDGE,"E6.bottom"),sQuery(id+"F3.wireOp",EDGE,"E10.filletArc")])]})});
            var Q96;
            Q96=makeQuery(id+"FRUT5MbfFa7QnNZ_1.6.F4.boolean.opBoolean","INTERSECT",EDGE,{"derivedFrom":[makeQuery(id+"F2.opShell","OFFSET_FACE",FACE,{"disambiguationData":[OSD([sQuery(id+"F0.wireOp",EDGE,"E4")])]}),makeQuery(id+"FRUT5MbfFa7QnNZ_1.6.F4.opExtrude","SWEPT_FACE",FACE,{"disambiguationData":[OSD([sQuery(id+"F3.wireOp",EDGE,"E6.bottom")])]})]});
            var Q97;
            Q97=makeQuery(id+"F4.boolean.opBoolean","COPY",EDGE,{"derivedFrom":makeQuery(id+"F4.opExtrude","SWEPT_EDGE",EDGE,{"disambiguationData":[OSD([sQuery(id+"F3.wireOp",EDGE,"E6.bottom"),sQuery(id+"F3.wireOp",EDGE,"E10.filletArc")])]})});
            var Q98;
            Q98=makeQuery(id+"FRUT5MbfFa7QnNZ_1.5.F4.boolean.opBoolean","COPY",EDGE,{"derivedFrom":makeQuery(id+"FRUT5MbfFa7QnNZ_1.5.F4.opExtrude","SWEPT_EDGE",EDGE,{"disambiguationData":[OSD([sQuery(id+"F3.wireOp",EDGE,"E6.top"),sQuery(id+"F3.wireOp",EDGE,"E8.filletArc")])]})});
            var Q99;
            Q99=makeQuery(id+"FRUT5MbfFa7QnNZ_1.1.F4.boolean.opBoolean","COPY",EDGE,{"derivedFrom":makeQuery(id+"FRUT5MbfFa7QnNZ_1.1.F4.opExtrude","SWEPT_EDGE",EDGE,{"disambiguationData":[OSD([sQuery(id+"F3.wireOp",EDGE,"E6.right"),sQuery(id+"F3.wireOp",EDGE,"E9.filletArc")])]})});
            var Q100;
            Q100=makeQuery(id+"FRUT5MbfFa7QnNZ_1.6.F4.boolean.opBoolean","INTERSECT",EDGE,{"derivedFrom":[makeQuery(id+"F2.opShell","OFFSET_FACE",FACE,{"disambiguationData":[OSD([sQuery(id+"F0.wireOp",EDGE,"E4")])]}),makeQuery(id+"FRUT5MbfFa7QnNZ_1.6.F4.opExtrude","SWEPT_FACE",FACE,{"disambiguationData":[OSD([sQuery(id+"F3.wireOp",EDGE,"E6.left")])]})]});
            var Q101;
            Q101=makeQuery(id+"F4.boolean.opBoolean","COPY",EDGE,{"derivedFrom":makeQuery(id+"F4.opExtrude","SWEPT_EDGE",EDGE,{"disambiguationData":[OSD([sQuery(id+"F3.wireOp",EDGE,"E6.right"),sQuery(id+"F3.wireOp",EDGE,"E7.filletArc")])]})});
            var Q102;
            Q102=makeQuery(id+"F4.boolean.opBoolean","INTERSECT",EDGE,{"derivedFrom":[makeQuery(id+"F2.opShell","OFFSET_FACE",FACE,{"disambiguationData":[OSD([sQuery(id+"F0.wireOp",EDGE,"E4")])]}),makeQuery(id+"F4.opExtrude","SWEPT_FACE",FACE,{"disambiguationData":[OSD([sQuery(id+"F3.wireOp",EDGE,"E6.bottom")])]})]});
            var Q103;
            Q103=makeQuery(id+"FRUT5MbfFa7QnNZ_1.5.F4.boolean.opBoolean","COPY",EDGE,{"derivedFrom":makeQuery(id+"FRUT5MbfFa7QnNZ_1.5.F4.opExtrude","SWEPT_EDGE",EDGE,{"disambiguationData":[OSD([sQuery(id+"F3.wireOp",EDGE,"E6.left"),sQuery(id+"F3.wireOp",EDGE,"E8.filletArc")])]})});
            var Q104;
            Q104=makeQuery(id+"FRUT5MbfFa7QnNZ_1.6.F4.boolean.opBoolean","COPY",EDGE,{"derivedFrom":makeQuery(id+"FRUT5MbfFa7QnNZ_1.6.F4.opExtrude","SWEPT_EDGE",EDGE,{"disambiguationData":[OSD([sQuery(id+"F3.wireOp",EDGE,"E6.left"),sQuery(id+"F3.wireOp",EDGE,"E10.filletArc")])]})});
            var Q105;
            Q105=makeQuery(id+"FRUT5MbfFa7QnNZ_1.4.F4.boolean.opBoolean","COPY",EDGE,{"derivedFrom":makeQuery(id+"FRUT5MbfFa7QnNZ_1.4.F4.opExtrude","SWEPT_EDGE",EDGE,{"disambiguationData":[OSD([sQuery(id+"F3.wireOp",EDGE,"E6.top"),sQuery(id+"F3.wireOp",EDGE,"E7.filletArc")])]})});
            var Q106;
            Q106=makeQuery(id+"FRUT5MbfFa7QnNZ_1.5.F4.boolean.opBoolean","COPY",EDGE,{"derivedFrom":makeQuery(id+"FRUT5MbfFa7QnNZ_1.5.F4.opExtrude","SWEPT_EDGE",EDGE,{"disambiguationData":[OSD([sQuery(id+"F3.wireOp",EDGE,"E6.right"),sQuery(id+"F3.wireOp",EDGE,"E9.filletArc")])]})});
            var Q107;
            Q107=makeQuery(id+"FRUT5MbfFa7QnNZ_1.1.F4.boolean.opBoolean","INTERSECT",EDGE,{"derivedFrom":[makeQuery(id+"F2.opShell","OFFSET_FACE",FACE,{"disambiguationData":[OSD([sQuery(id+"F0.wireOp",EDGE,"E4")])]}),makeQuery(id+"FRUT5MbfFa7QnNZ_1.1.F4.opExtrude","SWEPT_FACE",FACE,{"disambiguationData":[OSD([sQuery(id+"F3.wireOp",EDGE,"E7.filletArc")])]})]});
            var Q108;
            Q108=makeQuery(id+"FRUT5MbfFa7QnNZ_1.5.F4.boolean.opBoolean","INTERSECT",EDGE,{"derivedFrom":[makeQuery(id+"F2.opShell","OFFSET_FACE",FACE,{"disambiguationData":[OSD([sQuery(id+"F0.wireOp",EDGE,"E4")])]}),makeQuery(id+"FRUT5MbfFa7QnNZ_1.5.F4.opExtrude","SWEPT_FACE",FACE,{"disambiguationData":[OSD([sQuery(id+"F3.wireOp",EDGE,"E6.right")])]})]});
            var Q109;
            Q109=makeQuery(id+"FRUT5MbfFa7QnNZ_1.5.F4.boolean.opBoolean","INTERSECT",EDGE,{"derivedFrom":[makeQuery(id+"F2.opShell","OFFSET_FACE",FACE,{"disambiguationData":[OSD([sQuery(id+"F0.wireOp",EDGE,"E4")])]}),makeQuery(id+"FRUT5MbfFa7QnNZ_1.5.F4.opExtrude","SWEPT_FACE",FACE,{"disambiguationData":[OSD([sQuery(id+"F3.wireOp",EDGE,"E8.filletArc")])]})]});
            var Q110;
            Q110=makeQuery(id+"FRUT5MbfFa7QnNZ_1.2.F4.boolean.opBoolean","COPY",EDGE,{"derivedFrom":makeQuery(id+"FRUT5MbfFa7QnNZ_1.2.F4.opExtrude","SWEPT_EDGE",EDGE,{"disambiguationData":[OSD([sQuery(id+"F3.wireOp",EDGE,"E6.top"),sQuery(id+"F3.wireOp",EDGE,"E8.filletArc")])]})});
            var Q111;
            Q111=makeQuery(id+"FRUT5MbfFa7QnNZ_1.4.F4.boolean.opBoolean","COPY",EDGE,{"derivedFrom":makeQuery(id+"FRUT5MbfFa7QnNZ_1.4.F4.opExtrude","SWEPT_EDGE",EDGE,{"disambiguationData":[OSD([sQuery(id+"F3.wireOp",EDGE,"E6.bottom"),sQuery(id+"F3.wireOp",EDGE,"E10.filletArc")])]})});
            var Q112;
            Q112=makeQuery(id+"F4.boolean.opBoolean","INTERSECT",EDGE,{"derivedFrom":[makeQuery(id+"F2.opShell","OFFSET_FACE",FACE,{"disambiguationData":[OSD([sQuery(id+"F0.wireOp",EDGE,"E4")])]}),makeQuery(id+"F4.opExtrude","SWEPT_FACE",FACE,{"disambiguationData":[OSD([sQuery(id+"F3.wireOp",EDGE,"E7.filletArc")])]})]});
            var Q113;
            Q113=makeQuery(id+"FRUT5MbfFa7QnNZ_1.6.F4.boolean.opBoolean","INTERSECT",EDGE,{"derivedFrom":[makeQuery(id+"F1.opRevolve","SWEPT_FACE",FACE,{"disambiguationData":[OSD([sQuery(id+"F0.wireOp",EDGE,"E4")])]}),makeQuery(id+"FRUT5MbfFa7QnNZ_1.6.F4.opExtrude","SWEPT_FACE",FACE,{"disambiguationData":[OSD([sQuery(id+"F3.wireOp",EDGE,"E7.filletArc")])]})]});
            var Q114;
            Q114=makeQuery(id+"FRUT5MbfFa7QnNZ_1.2.F4.boolean.opBoolean","INTERSECT",EDGE,{"derivedFrom":[makeQuery(id+"F2.opShell","OFFSET_FACE",FACE,{"disambiguationData":[OSD([sQuery(id+"F0.wireOp",EDGE,"E4")])]}),makeQuery(id+"FRUT5MbfFa7QnNZ_1.2.F4.opExtrude","SWEPT_FACE",FACE,{"disambiguationData":[OSD([sQuery(id+"F3.wireOp",EDGE,"E7.filletArc")])]})]});
            var Q115;
            Q115=makeQuery(id+"FRUT5MbfFa7QnNZ_1.3.F4.boolean.opBoolean","INTERSECT",EDGE,{"derivedFrom":[makeQuery(id+"F2.opShell","OFFSET_FACE",FACE,{"disambiguationData":[OSD([sQuery(id+"F0.wireOp",EDGE,"E4")])]}),makeQuery(id+"FRUT5MbfFa7QnNZ_1.3.F4.opExtrude","SWEPT_FACE",FACE,{"disambiguationData":[OSD([sQuery(id+"F3.wireOp",EDGE,"E6.right")])]})]});
            var Q116;
            Q116=makeQuery(id+"FRUT5MbfFa7QnNZ_1.5.F4.boolean.opBoolean","COPY",EDGE,{"derivedFrom":makeQuery(id+"FRUT5MbfFa7QnNZ_1.5.F4.opExtrude","SWEPT_EDGE",EDGE,{"disambiguationData":[OSD([sQuery(id+"F3.wireOp",EDGE,"E6.bottom"),sQuery(id+"F3.wireOp",EDGE,"E9.filletArc")])]})});
            var Q117;
            Q117=makeQuery(id+"FRUT5MbfFa7QnNZ_1.5.F4.boolean.opBoolean","INTERSECT",EDGE,{"derivedFrom":[makeQuery(id+"F2.opShell","OFFSET_FACE",FACE,{"disambiguationData":[OSD([sQuery(id+"F0.wireOp",EDGE,"E4")])]}),makeQuery(id+"FRUT5MbfFa7QnNZ_1.5.F4.opExtrude","SWEPT_FACE",FACE,{"disambiguationData":[OSD([sQuery(id+"F3.wireOp",EDGE,"E7.filletArc")])]})]});
            var Q118;
            Q118=makeQuery(id+"FRUT5MbfFa7QnNZ_1.4.F4.boolean.opBoolean","INTERSECT",EDGE,{"derivedFrom":[makeQuery(id+"F2.opShell","OFFSET_FACE",FACE,{"disambiguationData":[OSD([sQuery(id+"F0.wireOp",EDGE,"E4")])]}),makeQuery(id+"FRUT5MbfFa7QnNZ_1.4.F4.opExtrude","SWEPT_FACE",FACE,{"disambiguationData":[OSD([sQuery(id+"F3.wireOp",EDGE,"E9.filletArc")])]})]});
            var Q119;
            Q119=makeQuery(id+"FRUT5MbfFa7QnNZ_1.2.F4.boolean.opBoolean","INTERSECT",EDGE,{"derivedFrom":[makeQuery(id+"F2.opShell","OFFSET_FACE",FACE,{"disambiguationData":[OSD([sQuery(id+"F0.wireOp",EDGE,"E4")])]}),makeQuery(id+"FRUT5MbfFa7QnNZ_1.2.F4.opExtrude","SWEPT_FACE",FACE,{"disambiguationData":[OSD([sQuery(id+"F3.wireOp",EDGE,"E8.filletArc")])]})]});
            var Q120;
            Q120=makeQuery(id+"F4.boolean.opBoolean","INTERSECT",EDGE,{"derivedFrom":[makeQuery(id+"F2.opShell","OFFSET_FACE",FACE,{"disambiguationData":[OSD([sQuery(id+"F0.wireOp",EDGE,"E4")])]}),makeQuery(id+"F4.opExtrude","SWEPT_FACE",FACE,{"disambiguationData":[OSD([sQuery(id+"F3.wireOp",EDGE,"E10.filletArc")])]})]});
            var Q121;
            Q121=makeQuery(id+"FRUT5MbfFa7QnNZ_1.4.F4.boolean.opBoolean","COPY",EDGE,{"derivedFrom":makeQuery(id+"FRUT5MbfFa7QnNZ_1.4.F4.opExtrude","SWEPT_EDGE",EDGE,{"disambiguationData":[OSD([sQuery(id+"F3.wireOp",EDGE,"E6.right"),sQuery(id+"F3.wireOp",EDGE,"E9.filletArc")])]})});
            var Q122;
            Q122=makeQuery(id+"FRUT5MbfFa7QnNZ_1.1.F4.boolean.opBoolean","INTERSECT",EDGE,{"derivedFrom":[makeQuery(id+"F2.opShell","OFFSET_FACE",FACE,{"disambiguationData":[OSD([sQuery(id+"F0.wireOp",EDGE,"E4")])]}),makeQuery(id+"FRUT5MbfFa7QnNZ_1.1.F4.opExtrude","SWEPT_FACE",FACE,{"disambiguationData":[OSD([sQuery(id+"F3.wireOp",EDGE,"E6.left")])]})]});
            var Q123;
            Q123=makeQuery(id+"FRUT5MbfFa7QnNZ_1.3.F4.boolean.opBoolean","COPY",EDGE,{"derivedFrom":makeQuery(id+"FRUT5MbfFa7QnNZ_1.3.F4.opExtrude","SWEPT_EDGE",EDGE,{"disambiguationData":[OSD([sQuery(id+"F3.wireOp",EDGE,"E6.top"),sQuery(id+"F3.wireOp",EDGE,"E8.filletArc")])]})});
            var Q124;
            Q124=makeQuery(id+"FRUT5MbfFa7QnNZ_1.2.F4.boolean.opBoolean","INTERSECT",EDGE,{"derivedFrom":[makeQuery(id+"F1.opRevolve","SWEPT_FACE",FACE,{"disambiguationData":[OSD([sQuery(id+"F0.wireOp",EDGE,"E4")])]}),makeQuery(id+"FRUT5MbfFa7QnNZ_1.2.F4.opExtrude","SWEPT_FACE",FACE,{"disambiguationData":[OSD([sQuery(id+"F3.wireOp",EDGE,"E8.filletArc")])]})]});
            var Q125;
            Q125=makeQuery(id+"FRUT5MbfFa7QnNZ_1.3.F4.boolean.opBoolean","INTERSECT",EDGE,{"derivedFrom":[makeQuery(id+"F1.opRevolve","SWEPT_FACE",FACE,{"disambiguationData":[OSD([sQuery(id+"F0.wireOp",EDGE,"E4")])]}),makeQuery(id+"FRUT5MbfFa7QnNZ_1.3.F4.opExtrude","SWEPT_FACE",FACE,{"disambiguationData":[OSD([sQuery(id+"F3.wireOp",EDGE,"E8.filletArc")])]})]});
            var Q126;
            Q126=makeQuery(id+"FRUT5MbfFa7QnNZ_1.4.F4.boolean.opBoolean","INTERSECT",EDGE,{"derivedFrom":[makeQuery(id+"F1.opRevolve","SWEPT_FACE",FACE,{"disambiguationData":[OSD([sQuery(id+"F0.wireOp",EDGE,"E4")])]}),makeQuery(id+"FRUT5MbfFa7QnNZ_1.4.F4.opExtrude","SWEPT_FACE",FACE,{"disambiguationData":[OSD([sQuery(id+"F3.wireOp",EDGE,"E8.filletArc")])]})]});
            var Q127;
            Q127=makeQuery(id+"FRUT5MbfFa7QnNZ_1.5.F4.boolean.opBoolean","INTERSECT",EDGE,{"derivedFrom":[makeQuery(id+"F1.opRevolve","SWEPT_FACE",FACE,{"disambiguationData":[OSD([sQuery(id+"F0.wireOp",EDGE,"E4")])]}),makeQuery(id+"FRUT5MbfFa7QnNZ_1.5.F4.opExtrude","SWEPT_FACE",FACE,{"disambiguationData":[OSD([sQuery(id+"F3.wireOp",EDGE,"E8.filletArc")])]})]});
            var Q128;
            Q128=makeQuery(id+"FRUT5MbfFa7QnNZ_1.5.F4.boolean.opBoolean","INTERSECT",EDGE,{"derivedFrom":[makeQuery(id+"F1.opRevolve","SWEPT_FACE",FACE,{"disambiguationData":[OSD([sQuery(id+"F0.wireOp",EDGE,"E4")])]}),makeQuery(id+"FRUT5MbfFa7QnNZ_1.5.F4.opExtrude","SWEPT_FACE",FACE,{"disambiguationData":[OSD([sQuery(id+"F3.wireOp",EDGE,"E10.filletArc")])]})]});
            var Q129;
            Q129=makeQuery(id+"FRUT5MbfFa7QnNZ_1.1.F4.boolean.opBoolean","INTERSECT",EDGE,{"derivedFrom":[makeQuery(id+"F1.opRevolve","SWEPT_FACE",FACE,{"disambiguationData":[OSD([sQuery(id+"F0.wireOp",EDGE,"E4")])]}),makeQuery(id+"FRUT5MbfFa7QnNZ_1.1.F4.opExtrude","SWEPT_FACE",FACE,{"disambiguationData":[OSD([sQuery(id+"F3.wireOp",EDGE,"E6.bottom")])]})]});
            var Q130;
            Q130=makeQuery(id+"FRUT5MbfFa7QnNZ_1.1.F4.boolean.opBoolean","INTERSECT",EDGE,{"derivedFrom":[makeQuery(id+"F1.opRevolve","SWEPT_FACE",FACE,{"disambiguationData":[OSD([sQuery(id+"F0.wireOp",EDGE,"E4")])]}),makeQuery(id+"FRUT5MbfFa7QnNZ_1.1.F4.opExtrude","SWEPT_FACE",FACE,{"disambiguationData":[OSD([sQuery(id+"F3.wireOp",EDGE,"E6.top")])]})]});
            var Q131;
            Q131=makeQuery(id+"FRUT5MbfFa7QnNZ_1.2.F4.boolean.opBoolean","INTERSECT",EDGE,{"derivedFrom":[makeQuery(id+"F1.opRevolve","SWEPT_FACE",FACE,{"disambiguationData":[OSD([sQuery(id+"F0.wireOp",EDGE,"E4")])]}),makeQuery(id+"FRUT5MbfFa7QnNZ_1.2.F4.opExtrude","SWEPT_FACE",FACE,{"disambiguationData":[OSD([sQuery(id+"F3.wireOp",EDGE,"E6.bottom")])]})]});
            var Q132;
            Q132=makeQuery(id+"FRUT5MbfFa7QnNZ_1.2.F4.boolean.opBoolean","INTERSECT",EDGE,{"derivedFrom":[makeQuery(id+"F1.opRevolve","SWEPT_FACE",FACE,{"disambiguationData":[OSD([sQuery(id+"F0.wireOp",EDGE,"E4")])]}),makeQuery(id+"FRUT5MbfFa7QnNZ_1.2.F4.opExtrude","SWEPT_FACE",FACE,{"disambiguationData":[OSD([sQuery(id+"F3.wireOp",EDGE,"E6.left")])]})]});
            var Q133;
            Q133=makeQuery(id+"FRUT5MbfFa7QnNZ_1.3.F4.boolean.opBoolean","INTERSECT",EDGE,{"derivedFrom":[makeQuery(id+"F1.opRevolve","SWEPT_FACE",FACE,{"disambiguationData":[OSD([sQuery(id+"F0.wireOp",EDGE,"E4")])]}),makeQuery(id+"FRUT5MbfFa7QnNZ_1.3.F4.opExtrude","SWEPT_FACE",FACE,{"disambiguationData":[OSD([sQuery(id+"F3.wireOp",EDGE,"E6.right")])]})]});
            var Q134;
            Q134=makeQuery(id+"FRUT5MbfFa7QnNZ_1.3.F4.boolean.opBoolean","INTERSECT",EDGE,{"derivedFrom":[makeQuery(id+"F1.opRevolve","SWEPT_FACE",FACE,{"disambiguationData":[OSD([sQuery(id+"F0.wireOp",EDGE,"E4")])]}),makeQuery(id+"FRUT5MbfFa7QnNZ_1.3.F4.opExtrude","SWEPT_FACE",FACE,{"disambiguationData":[OSD([sQuery(id+"F3.wireOp",EDGE,"E6.bottom")])]})]});
            var Q135;
            Q135=makeQuery(id+"FRUT5MbfFa7QnNZ_1.1.F4.boolean.opBoolean","INTERSECT",EDGE,{"derivedFrom":[makeQuery(id+"F1.opRevolve","SWEPT_FACE",FACE,{"disambiguationData":[OSD([sQuery(id+"F0.wireOp",EDGE,"E4")])]}),makeQuery(id+"FRUT5MbfFa7QnNZ_1.1.F4.opExtrude","SWEPT_FACE",FACE,{"disambiguationData":[OSD([sQuery(id+"F3.wireOp",EDGE,"E6.left")])]})]});
            var Q136;
            Q136=makeQuery(id+"FRUT5MbfFa7QnNZ_1.4.F4.boolean.opBoolean","COPY",EDGE,{"derivedFrom":makeQuery(id+"FRUT5MbfFa7QnNZ_1.4.F4.opExtrude","SWEPT_EDGE",EDGE,{"disambiguationData":[OSD([sQuery(id+"F3.wireOp",EDGE,"E6.left"),sQuery(id+"F3.wireOp",EDGE,"E10.filletArc")])]})});
            var Q137;
            Q137=makeQuery(id+"FRUT5MbfFa7QnNZ_1.2.F4.boolean.opBoolean","COPY",EDGE,{"derivedFrom":makeQuery(id+"FRUT5MbfFa7QnNZ_1.2.F4.opExtrude","SWEPT_EDGE",EDGE,{"disambiguationData":[OSD([sQuery(id+"F3.wireOp",EDGE,"E6.left"),sQuery(id+"F3.wireOp",EDGE,"E8.filletArc")])]})});
            var Q138;
            Q138=makeQuery(id+"F4.boolean.opBoolean","COPY",EDGE,{"derivedFrom":makeQuery(id+"F4.opExtrude","SWEPT_EDGE",EDGE,{"disambiguationData":[OSD([sQuery(id+"F3.wireOp",EDGE,"E6.left"),sQuery(id+"F3.wireOp",EDGE,"E8.filletArc")])]})});
            var Q139;
            Q139=makeQuery(id+"FRUT5MbfFa7QnNZ_1.4.F4.boolean.opBoolean","INTERSECT",EDGE,{"derivedFrom":[makeQuery(id+"F2.opShell","OFFSET_FACE",FACE,{"disambiguationData":[OSD([sQuery(id+"F0.wireOp",EDGE,"E4")])]}),makeQuery(id+"FRUT5MbfFa7QnNZ_1.4.F4.opExtrude","SWEPT_FACE",FACE,{"disambiguationData":[OSD([sQuery(id+"F3.wireOp",EDGE,"E10.filletArc")])]})]});
            var Q140;
            Q140=makeQuery(id+"FRUT5MbfFa7QnNZ_1.3.F4.boolean.opBoolean","COPY",EDGE,{"derivedFrom":makeQuery(id+"FRUT5MbfFa7QnNZ_1.3.F4.opExtrude","SWEPT_EDGE",EDGE,{"disambiguationData":[OSD([sQuery(id+"F3.wireOp",EDGE,"E6.right"),sQuery(id+"F3.wireOp",EDGE,"E7.filletArc")])]})});
            var Q141;
            Q141=makeQuery(id+"FRUT5MbfFa7QnNZ_1.6.F4.boolean.opBoolean","COPY",EDGE,{"derivedFrom":makeQuery(id+"FRUT5MbfFa7QnNZ_1.6.F4.opExtrude","SWEPT_EDGE",EDGE,{"disambiguationData":[OSD([sQuery(id+"F3.wireOp",EDGE,"E6.bottom"),sQuery(id+"F3.wireOp",EDGE,"E10.filletArc")])]})});
            var Q142;
            Q142=makeQuery(id+"FRUT5MbfFa7QnNZ_1.2.F4.boolean.opBoolean","INTERSECT",EDGE,{"derivedFrom":[makeQuery(id+"F2.opShell","OFFSET_FACE",FACE,{"disambiguationData":[OSD([sQuery(id+"F0.wireOp",EDGE,"E4")])]}),makeQuery(id+"FRUT5MbfFa7QnNZ_1.2.F4.opExtrude","SWEPT_FACE",FACE,{"disambiguationData":[OSD([sQuery(id+"F3.wireOp",EDGE,"E9.filletArc")])]})]});
            var Q143;
            Q143=makeQuery(id+"FRUT5MbfFa7QnNZ_1.1.F4.boolean.opBoolean","COPY",EDGE,{"derivedFrom":makeQuery(id+"FRUT5MbfFa7QnNZ_1.1.F4.opExtrude","SWEPT_EDGE",EDGE,{"disambiguationData":[OSD([sQuery(id+"F3.wireOp",EDGE,"E6.left"),sQuery(id+"F3.wireOp",EDGE,"E8.filletArc")])]})});
            var Q144;
            Q144=makeQuery(id+"FRUT5MbfFa7QnNZ_1.1.F4.boolean.opBoolean","INTERSECT",EDGE,{"derivedFrom":[makeQuery(id+"F2.opShell","OFFSET_FACE",FACE,{"disambiguationData":[OSD([sQuery(id+"F0.wireOp",EDGE,"E4")])]}),makeQuery(id+"FRUT5MbfFa7QnNZ_1.1.F4.opExtrude","SWEPT_FACE",FACE,{"disambiguationData":[OSD([sQuery(id+"F3.wireOp",EDGE,"E8.filletArc")])]})]});
            var Q145;
            Q145=makeQuery(id+"FRUT5MbfFa7QnNZ_1.2.F4.boolean.opBoolean","COPY",EDGE,{"derivedFrom":makeQuery(id+"FRUT5MbfFa7QnNZ_1.2.F4.opExtrude","SWEPT_EDGE",EDGE,{"disambiguationData":[OSD([sQuery(id+"F3.wireOp",EDGE,"E6.bottom"),sQuery(id+"F3.wireOp",EDGE,"E10.filletArc")])]})});
            var Q146;
            Q146=makeQuery(id+"F4.boolean.opBoolean","INTERSECT",EDGE,{"derivedFrom":[makeQuery(id+"F2.opShell","OFFSET_FACE",FACE,{"disambiguationData":[OSD([sQuery(id+"F0.wireOp",EDGE,"E4")])]}),makeQuery(id+"F4.opExtrude","SWEPT_FACE",FACE,{"disambiguationData":[OSD([sQuery(id+"F3.wireOp",EDGE,"E9.filletArc")])]})]});
            var Q147;
            Q147=makeQuery(id+"FRUT5MbfFa7QnNZ_1.1.F4.boolean.opBoolean","COPY",EDGE,{"derivedFrom":makeQuery(id+"FRUT5MbfFa7QnNZ_1.1.F4.opExtrude","SWEPT_EDGE",EDGE,{"disambiguationData":[OSD([sQuery(id+"F3.wireOp",EDGE,"E6.left"),sQuery(id+"F3.wireOp",EDGE,"E10.filletArc")])]})});
            var Q148;
            Q148=makeQuery(id+"F4.boolean.opBoolean","COPY",EDGE,{"derivedFrom":makeQuery(id+"F4.opExtrude","SWEPT_EDGE",EDGE,{"disambiguationData":[OSD([sQuery(id+"F3.wireOp",EDGE,"E6.right"),sQuery(id+"F3.wireOp",EDGE,"E9.filletArc")])]})});
            var Q149;
            Q149=makeQuery(id+"FRUT5MbfFa7QnNZ_1.4.F4.boolean.opBoolean","INTERSECT",EDGE,{"derivedFrom":[makeQuery(id+"F1.opRevolve","SWEPT_FACE",FACE,{"disambiguationData":[OSD([sQuery(id+"F0.wireOp",EDGE,"E4")])]}),makeQuery(id+"FRUT5MbfFa7QnNZ_1.4.F4.opExtrude","SWEPT_FACE",FACE,{"disambiguationData":[OSD([sQuery(id+"F3.wireOp",EDGE,"E10.filletArc")])]})]});
            var Q150;
            Q150=makeQuery(id+"F4.boolean.opBoolean","INTERSECT",EDGE,{"derivedFrom":[makeQuery(id+"F1.opRevolve","SWEPT_FACE",FACE,{"disambiguationData":[OSD([sQuery(id+"F0.wireOp",EDGE,"E4")])]}),makeQuery(id+"F4.opExtrude","SWEPT_FACE",FACE,{"disambiguationData":[OSD([sQuery(id+"F3.wireOp",EDGE,"E8.filletArc")])]})]});
            var Q151;
            Q151=makeQuery(id+"F4.boolean.opBoolean","INTERSECT",EDGE,{"derivedFrom":[makeQuery(id+"F1.opRevolve","SWEPT_FACE",FACE,{"disambiguationData":[OSD([sQuery(id+"F0.wireOp",EDGE,"E4")])]}),makeQuery(id+"F4.opExtrude","SWEPT_FACE",FACE,{"disambiguationData":[OSD([sQuery(id+"F3.wireOp",EDGE,"E9.filletArc")])]})]});
            var Q152;
            Q152=makeQuery(id+"FRUT5MbfFa7QnNZ_1.1.F4.boolean.opBoolean","INTERSECT",EDGE,{"derivedFrom":[makeQuery(id+"F1.opRevolve","SWEPT_FACE",FACE,{"disambiguationData":[OSD([sQuery(id+"F0.wireOp",EDGE,"E4")])]}),makeQuery(id+"FRUT5MbfFa7QnNZ_1.1.F4.opExtrude","SWEPT_FACE",FACE,{"disambiguationData":[OSD([sQuery(id+"F3.wireOp",EDGE,"E8.filletArc")])]})]});
            var Q153;
            Q153=makeQuery(id+"FRUT5MbfFa7QnNZ_1.1.F4.boolean.opBoolean","INTERSECT",EDGE,{"derivedFrom":[makeQuery(id+"F1.opRevolve","SWEPT_FACE",FACE,{"disambiguationData":[OSD([sQuery(id+"F0.wireOp",EDGE,"E4")])]}),makeQuery(id+"FRUT5MbfFa7QnNZ_1.1.F4.opExtrude","SWEPT_FACE",FACE,{"disambiguationData":[OSD([sQuery(id+"F3.wireOp",EDGE,"E9.filletArc")])]})]});
            var Q154;
            Q154=makeQuery(id+"FRUT5MbfFa7QnNZ_1.1.F4.boolean.opBoolean","INTERSECT",EDGE,{"derivedFrom":[makeQuery(id+"F1.opRevolve","SWEPT_FACE",FACE,{"disambiguationData":[OSD([sQuery(id+"F0.wireOp",EDGE,"E4")])]}),makeQuery(id+"FRUT5MbfFa7QnNZ_1.1.F4.opExtrude","SWEPT_FACE",FACE,{"disambiguationData":[OSD([sQuery(id+"F3.wireOp",EDGE,"E10.filletArc")])]})]});
            var Q155;
            Q155=makeQuery(id+"FRUT5MbfFa7QnNZ_1.2.F4.boolean.opBoolean","INTERSECT",EDGE,{"derivedFrom":[makeQuery(id+"F1.opRevolve","SWEPT_FACE",FACE,{"disambiguationData":[OSD([sQuery(id+"F0.wireOp",EDGE,"E4")])]}),makeQuery(id+"FRUT5MbfFa7QnNZ_1.2.F4.opExtrude","SWEPT_FACE",FACE,{"disambiguationData":[OSD([sQuery(id+"F3.wireOp",EDGE,"E9.filletArc")])]})]});
            var Q156;
            Q156=makeQuery(id+"FRUT5MbfFa7QnNZ_1.3.F4.boolean.opBoolean","INTERSECT",EDGE,{"derivedFrom":[makeQuery(id+"F1.opRevolve","SWEPT_FACE",FACE,{"disambiguationData":[OSD([sQuery(id+"F0.wireOp",EDGE,"E4")])]}),makeQuery(id+"FRUT5MbfFa7QnNZ_1.3.F4.opExtrude","SWEPT_FACE",FACE,{"disambiguationData":[OSD([sQuery(id+"F3.wireOp",EDGE,"E9.filletArc")])]})]});
            var Q157;
            Q157=makeQuery(id+"FRUT5MbfFa7QnNZ_1.3.F4.boolean.opBoolean","INTERSECT",EDGE,{"derivedFrom":[makeQuery(id+"F1.opRevolve","SWEPT_FACE",FACE,{"disambiguationData":[OSD([sQuery(id+"F0.wireOp",EDGE,"E4")])]}),makeQuery(id+"FRUT5MbfFa7QnNZ_1.3.F4.opExtrude","SWEPT_FACE",FACE,{"disambiguationData":[OSD([sQuery(id+"F3.wireOp",EDGE,"E7.filletArc")])]})]});
            var Q158;
            Q158=makeQuery(id+"FRUT5MbfFa7QnNZ_1.3.F4.boolean.opBoolean","INTERSECT",EDGE,{"derivedFrom":[makeQuery(id+"F1.opRevolve","SWEPT_FACE",FACE,{"disambiguationData":[OSD([sQuery(id+"F0.wireOp",EDGE,"E4")])]}),makeQuery(id+"FRUT5MbfFa7QnNZ_1.3.F4.opExtrude","SWEPT_FACE",FACE,{"disambiguationData":[OSD([sQuery(id+"F3.wireOp",EDGE,"E10.filletArc")])]})]});
            var Q159;
            Q159=makeQuery(id+"F4.boolean.opBoolean","COPY",EDGE,{"derivedFrom":makeQuery(id+"F4.opExtrude","SWEPT_EDGE",EDGE,{"disambiguationData":[OSD([sQuery(id+"F3.wireOp",EDGE,"E6.top"),sQuery(id+"F3.wireOp",EDGE,"E8.filletArc")])]})});
            var Q160;
            Q160=makeQuery(id+"FRUT5MbfFa7QnNZ_1.2.F4.boolean.opBoolean","COPY",EDGE,{"derivedFrom":makeQuery(id+"FRUT5MbfFa7QnNZ_1.2.F4.opExtrude","SWEPT_EDGE",EDGE,{"disambiguationData":[OSD([sQuery(id+"F3.wireOp",EDGE,"E6.bottom"),sQuery(id+"F3.wireOp",EDGE,"E9.filletArc")])]})});
            var Q161;
            Q161=makeQuery(id+"FRUT5MbfFa7QnNZ_1.3.F4.boolean.opBoolean","COPY",EDGE,{"derivedFrom":makeQuery(id+"FRUT5MbfFa7QnNZ_1.3.F4.opExtrude","SWEPT_EDGE",EDGE,{"disambiguationData":[OSD([sQuery(id+"F3.wireOp",EDGE,"E6.bottom"),sQuery(id+"F3.wireOp",EDGE,"E10.filletArc")])]})});
            var Q162;
            Q162=makeQuery(id+"FRUT5MbfFa7QnNZ_1.1.F4.boolean.opBoolean","COPY",EDGE,{"derivedFrom":makeQuery(id+"FRUT5MbfFa7QnNZ_1.1.F4.opExtrude","SWEPT_EDGE",EDGE,{"disambiguationData":[OSD([sQuery(id+"F3.wireOp",EDGE,"E6.bottom"),sQuery(id+"F3.wireOp",EDGE,"E10.filletArc")])]})});
            var Q163;
            Q163=makeQuery(id+"F4.boolean.opBoolean","INTERSECT",EDGE,{"derivedFrom":[makeQuery(id+"F2.opShell","OFFSET_FACE",FACE,{"disambiguationData":[OSD([sQuery(id+"F0.wireOp",EDGE,"E4")])]}),makeQuery(id+"F4.opExtrude","SWEPT_FACE",FACE,{"disambiguationData":[OSD([sQuery(id+"F3.wireOp",EDGE,"E8.filletArc")])]})]});
            var Q164;
            Q164=makeQuery(id+"FRUT5MbfFa7QnNZ_1.6.F4.boolean.opBoolean","COPY",EDGE,{"derivedFrom":makeQuery(id+"FRUT5MbfFa7QnNZ_1.6.F4.opExtrude","SWEPT_EDGE",EDGE,{"disambiguationData":[OSD([sQuery(id+"F3.wireOp",EDGE,"E6.bottom"),sQuery(id+"F3.wireOp",EDGE,"E9.filletArc")])]})});
            var Q165;
            Q165=makeQuery(id+"FRUT5MbfFa7QnNZ_1.2.F4.boolean.opBoolean","COPY",EDGE,{"derivedFrom":makeQuery(id+"FRUT5MbfFa7QnNZ_1.2.F4.opExtrude","SWEPT_EDGE",EDGE,{"disambiguationData":[OSD([sQuery(id+"F3.wireOp",EDGE,"E6.left"),sQuery(id+"F3.wireOp",EDGE,"E10.filletArc")])]})});
            var Q166;
            Q166=makeQuery(id+"FRUT5MbfFa7QnNZ_1.1.F4.boolean.opBoolean","INTERSECT",EDGE,{"derivedFrom":[makeQuery(id+"F2.opShell","OFFSET_FACE",FACE,{"disambiguationData":[OSD([sQuery(id+"F0.wireOp",EDGE,"E4")])]}),makeQuery(id+"FRUT5MbfFa7QnNZ_1.1.F4.opExtrude","SWEPT_FACE",FACE,{"disambiguationData":[OSD([sQuery(id+"F3.wireOp",EDGE,"E10.filletArc")])]})]});
            var Q167;
            Q167=makeQuery(id+"F4.boolean.opBoolean","COPY",EDGE,{"derivedFrom":makeQuery(id+"F4.opExtrude","SWEPT_EDGE",EDGE,{"disambiguationData":[OSD([sQuery(id+"F3.wireOp",EDGE,"E6.bottom"),sQuery(id+"F3.wireOp",EDGE,"E9.filletArc")])]})});
            var Q168;
            Q168=makeQuery(id+"FRUT5MbfFa7QnNZ_1.3.F4.boolean.opBoolean","INTERSECT",EDGE,{"derivedFrom":[makeQuery(id+"F2.opShell","OFFSET_FACE",FACE,{"disambiguationData":[OSD([sQuery(id+"F0.wireOp",EDGE,"E4")])]}),makeQuery(id+"FRUT5MbfFa7QnNZ_1.3.F4.opExtrude","SWEPT_FACE",FACE,{"disambiguationData":[OSD([sQuery(id+"F3.wireOp",EDGE,"E9.filletArc")])]})]});
            var Q169;
            Q169=makeQuery(id+"FRUT5MbfFa7QnNZ_1.3.F4.boolean.opBoolean","INTERSECT",EDGE,{"derivedFrom":[makeQuery(id+"F2.opShell","OFFSET_FACE",FACE,{"disambiguationData":[OSD([sQuery(id+"F0.wireOp",EDGE,"E4")])]}),makeQuery(id+"FRUT5MbfFa7QnNZ_1.3.F4.opExtrude","SWEPT_FACE",FACE,{"disambiguationData":[OSD([sQuery(id+"F3.wireOp",EDGE,"E7.filletArc")])]})]});
            var Q170;
            Q170=makeQuery(id+"FRUT5MbfFa7QnNZ_1.3.F4.boolean.opBoolean","COPY",EDGE,{"derivedFrom":makeQuery(id+"FRUT5MbfFa7QnNZ_1.3.F4.opExtrude","SWEPT_EDGE",EDGE,{"disambiguationData":[OSD([sQuery(id+"F3.wireOp",EDGE,"E6.right"),sQuery(id+"F3.wireOp",EDGE,"E9.filletArc")])]})});
            var Q171;
            Q171=makeQuery(id+"FRUT5MbfFa7QnNZ_1.1.F4.boolean.opBoolean","COPY",EDGE,{"derivedFrom":makeQuery(id+"FRUT5MbfFa7QnNZ_1.1.F4.opExtrude","SWEPT_EDGE",EDGE,{"disambiguationData":[OSD([sQuery(id+"F3.wireOp",EDGE,"E6.bottom"),sQuery(id+"F3.wireOp",EDGE,"E9.filletArc")])]})});
            var Q172;
            Q172=makeQuery(id+"FRUT5MbfFa7QnNZ_1.1.F4.boolean.opBoolean","COPY",EDGE,{"derivedFrom":makeQuery(id+"FRUT5MbfFa7QnNZ_1.1.F4.opExtrude","SWEPT_EDGE",EDGE,{"disambiguationData":[OSD([sQuery(id+"F3.wireOp",EDGE,"E6.top"),sQuery(id+"F3.wireOp",EDGE,"E8.filletArc")])]})});
            var Q173;
            Q173=makeQuery(id+"FRUT5MbfFa7QnNZ_1.3.F4.boolean.opBoolean","COPY",EDGE,{"derivedFrom":makeQuery(id+"FRUT5MbfFa7QnNZ_1.3.F4.opExtrude","SWEPT_EDGE",EDGE,{"disambiguationData":[OSD([sQuery(id+"F3.wireOp",EDGE,"E6.bottom"),sQuery(id+"F3.wireOp",EDGE,"E9.filletArc")])]})});
            var Q174;
            Q174=makeQuery(id+"FRUT5MbfFa7QnNZ_1.3.F4.boolean.opBoolean","COPY",EDGE,{"derivedFrom":makeQuery(id+"FRUT5MbfFa7QnNZ_1.3.F4.opExtrude","SWEPT_EDGE",EDGE,{"disambiguationData":[OSD([sQuery(id+"F3.wireOp",EDGE,"E6.top"),sQuery(id+"F3.wireOp",EDGE,"E7.filletArc")])]})});
            var Q175;
            Q175=makeQuery(id+"FRUT5MbfFa7QnNZ_1.2.F4.boolean.opBoolean","COPY",EDGE,{"derivedFrom":makeQuery(id+"FRUT5MbfFa7QnNZ_1.2.F4.opExtrude","SWEPT_EDGE",EDGE,{"disambiguationData":[OSD([sQuery(id+"F3.wireOp",EDGE,"E6.right"),sQuery(id+"F3.wireOp",EDGE,"E9.filletArc")])]})});
            fillet(context, id + "F5", {"entities" : qUnion([Q0, Q1, Q2, Q3, Q4, Q5, Q6, Q7, Q8, Q9, Q10, Q11, Q12, Q13, Q14, Q15, Q16, Q17, Q18, Q19, Q20, Q21, Q22, Q23, Q24, Q25, Q26, Q27, Q28, Q29, Q30, Q31, Q32, Q33, Q34, Q35, Q36, Q37, Q38, Q39, Q40, Q41, Q42, Q43, Q44, Q45, Q46, Q47, Q48, Q49, Q50, Q51, Q52, Q53, Q54, Q55, Q56, Q57, Q58, Q59, Q60, Q61, Q62, Q63, Q64, Q65, Q66, Q67, Q68, Q69, Q70, Q71, Q72, Q73, Q74, Q75, Q76, Q77, Q78, Q79, Q80, Q81, Q82, Q83, Q84, Q85, Q86, Q87, Q88, Q89, Q90, Q91, Q92, Q93, Q94, Q95, Q96, Q97, Q98, Q99, Q100, Q101, Q102, Q103, Q104, Q105, Q106, Q107, Q108, Q109, Q110, Q111, Q112, Q113, Q114, Q115, Q116, Q117, Q118, Q119, Q120, Q121, Q122, Q123, Q124, Q125, Q126, Q127, Q128, Q129, Q130, Q131, Q132, Q133, Q134, Q135, Q136, Q137, Q138, Q139, Q140, Q141, Q142, Q143, Q144, Q145, Q146, Q147, Q148, Q149, Q150, Q151, Q152, Q153, Q154, Q155, Q156, Q157, Q158, Q159, Q160, Q161, Q162, Q163, Q164, Q165, Q166, Q167, Q168, Q169, Q170, Q171, Q172, Q173, Q174, Q175]), "radius" : .15 * mm, "tangentPropagation" : true, "allowEdgeOverflow" : false});
        }
    });
